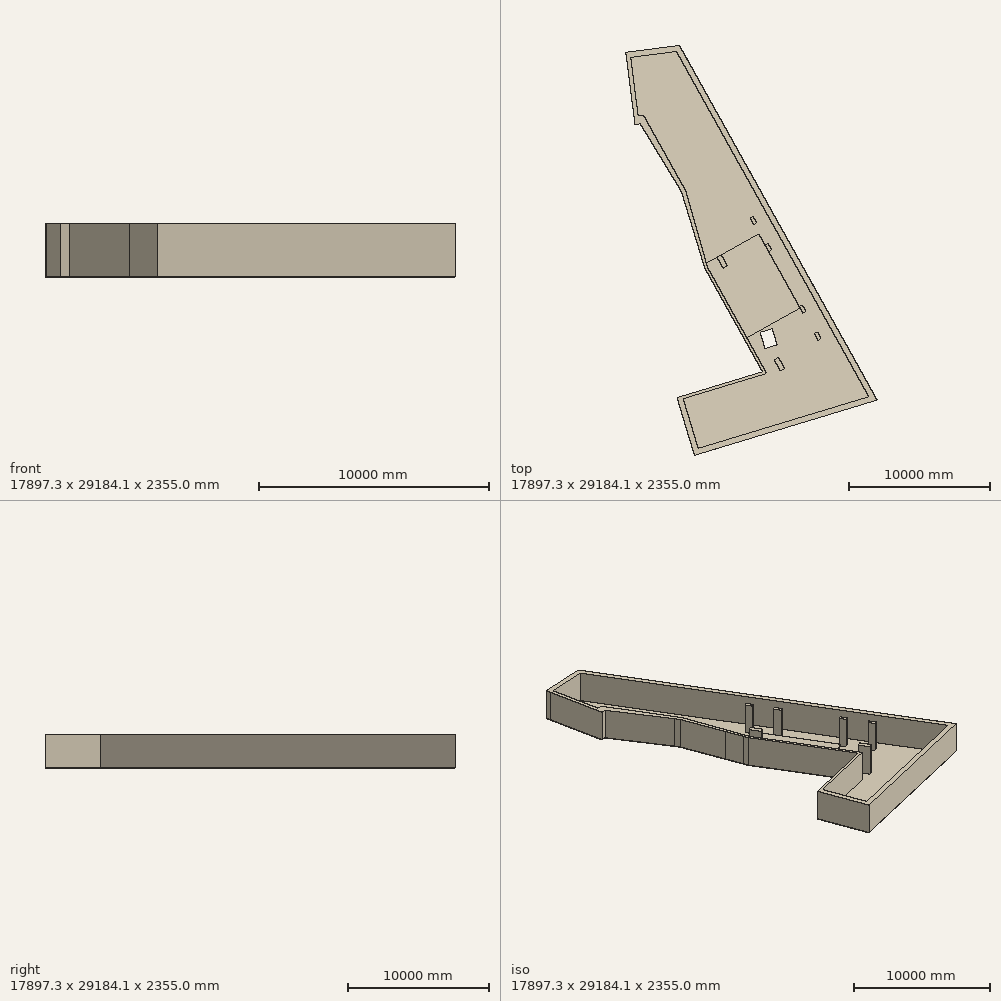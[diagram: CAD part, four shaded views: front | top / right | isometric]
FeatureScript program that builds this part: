
annotation { "Feature Type Name" : "Feature", "Feature Type Description" : "" }
export const myFeature = defineFeature(function(context is Context, id is Id, definition is map)
    precondition{}
    {
        {
            assignVariable(context, id + "F0", {"name" : "Ceiling", "anyValue" : 1890 + 440});
        }
        {
            var Q0;
            Q0=qCreatedBy(makeId("Top.planeOp"),FACE);
            var sketch = newSketch(context, id + "F1", { "sketchPlane" : qUnion([Q0])});
            skLineSegment(sketch, "E0", {"start": v(50356.24, 60225.68) * mm, "end": v(49220.2, 59881.82) * mm});
            skLineSegment(sketch, "E1", {"start": v(49220.2, 59881.82) * mm, "end": v(48658.24, 61738.46) * mm});
            skLineSegment(sketch, "E2", {"start": v(48658.24, 61738.46) * mm, "end": v(48436.53, 61671.35) * mm});
            skLineSegment(sketch, "E3", {"start": v(48436.53, 61671.35) * mm, "end": v(48364.1, 61910.63) * mm});
            skLineSegment(sketch, "E4", {"start": v(48364.1, 61910.63) * mm, "end": v(47885.55, 61765.78) * mm});
            skLineSegment(sketch, "E5", {"start": v(47885.55, 61765.78) * mm, "end": v(47957.97, 61526.5) * mm});
            skLineSegment(sketch, "E6", {"start": v(47957.97, 61526.5) * mm, "end": v(47686.86, 61444.44) * mm});
            skLineSegment(sketch, "E7", {"start": v(47686.86, 61444.44) * mm, "end": v(47759.29, 61205.16) * mm});
            skLineSegment(sketch, "E8", {"start": v(47759.29, 61205.16) * mm, "end": v(48491.38, 61426.75) * mm});
            skLineSegment(sketch, "E9", {"start": v(48491.38, 61426.75) * mm, "end": v(49070.78, 59512.52) * mm});
            skLineSegment(sketch, "E10", {"start": v(49070.78, 59512.52) * mm, "end": v(46721.47, 58801.43) * mm});
            skLineSegment(sketch, "E11", {"start": v(46721.47, 58801.43) * mm, "end": v(46142.07, 60715.66) * mm});
            skLineSegment(sketch, "E12", {"start": v(46142.07, 60715.66) * mm, "end": v(46706.46, 60886.5) * mm});
            skLineSegment(sketch, "E13", {"start": v(46706.46, 60886.5) * mm, "end": v(46634.03, 61125.77) * mm});
            skLineSegment(sketch, "E14", {"start": v(46634.03, 61125.77) * mm, "end": v(45451.68, 60767.9) * mm});
            skLineSegment(sketch, "E15", {"start": v(45451.68, 60767.9) * mm, "end": v(45524.1, 60528.62) * mm});
            skLineSegment(sketch, "E16", {"start": v(45524.1, 60528.62) * mm, "end": v(44643.85, 60262.18) * mm});
            skLineSegment(sketch, "E17", {"start": v(44643.85, 60262.18) * mm, "end": v(44571.42, 60501.46) * mm});
            skLineSegment(sketch, "E18", {"start": v(44571.42, 60501.46) * mm, "end": v(43824.87, 60275.5) * mm});
            skLineSegment(sketch, "E19", {"start": v(43824.87, 60275.5) * mm, "end": v(44386.83, 58418.88) * mm});
            skLineSegment(sketch, "E20", {"start": v(44386.83, 58418.88) * mm, "end": v(39132.43, 56828.48) * mm});
            skLineSegment(sketch, "E21", {"start": v(39132.43, 56828.48) * mm, "end": v(39132.43, 56828.48) * mm});
            skLineSegment(sketch, "E22", {"start": v(39132.43, 56828.48) * mm, "end": v(38458.91, 56624.62) * mm});
            skLineSegment(sketch, "E23", {"start": v(38458.91, 56624.62) * mm, "end": v(38574.8, 56241.77) * mm});
            skLineSegment(sketch, "E24", {"start": v(38574.8, 56241.77) * mm, "end": v(39350, 53680.63) * mm});
            skLineSegment(sketch, "E25", {"start": v(39350, 53680.63) * mm, "end": v(39348.17, 53681.01) * mm});
            skLineSegment(sketch, "E26", {"start": v(39348.17, 53681.01) * mm, "end": v(39517.02, 53123.18) * mm});
            skLineSegment(sketch, "E27", {"start": v(39517.02, 53123.18) * mm, "end": v(36984.61, 52356.67) * mm});
            skLineSegment(sketch, "E28", {"start": v(36984.61, 52356.67) * mm, "end": v(36288.15, 54657.64) * mm});
            skLineSegment(sketch, "E29", {"start": v(36288.15, 54657.64) * mm, "end": v(36288.98, 54657.9) * mm});
            skLineSegment(sketch, "E30", {"start": v(36288.98, 54657.9) * mm, "end": v(35925.26, 55857.73) * mm});
            skLineSegment(sketch, "E31", {"start": v(35925.26, 55857.73) * mm, "end": v(30957.21, 72270.12) * mm});
            skLineSegment(sketch, "E32", {"start": v(30957.21, 72270.12) * mm, "end": v(52856.55, 75078.33) * mm});
            skLineSegment(sketch, "E33", {"start": v(52856.55, 75078.33) * mm, "end": v(64538.41, 54127.57) * mm});
            skLineSegment(sketch, "E34", {"start": v(64538.41, 54127.57) * mm, "end": v(66559.72, 50502.1) * mm});
            skLineSegment(sketch, "E35", {"start": v(66559.72, 50502.1) * mm, "end": v(54412.26, 46825.31) * mm});
            skLineSegment(sketch, "E36", {"start": v(54412.26, 46825.31) * mm, "end": v(53342.81, 50358.57) * mm});
            skLineSegment(sketch, "E37", {"start": v(53342.81, 50358.57) * mm, "end": v(59288.18, 52158.11) * mm});
            skLineSegment(sketch, "E38", {"start": v(59288.18, 52158.11) * mm, "end": v(59106.76, 52483.52) * mm});
            skLineSegment(sketch, "E39", {"start": v(59106.76, 52483.52) * mm, "end": v(55867.2, 58292.84) * mm});
            skLineSegment(sketch, "E40", {"start": v(55867.2, 58292.84) * mm, "end": v(51354.69, 56926.99) * mm});
            skLineSegment(sketch, "E41", {"start": v(51354.69, 56926.99) * mm, "end": v(50356.24, 60225.68) * mm});
            skCircle(sketch, "E42", {"center": v(0, 0) * mm, "radius": 1927.6 * mm});
            skLineSegment(sketch, "E43", {"start": v(0, 5000) * mm, "end": v(0, -5000) * mm});
            skLineSegment(sketch, "E44", {"start": v(5000, 0) * mm, "end": v(-5000, 0) * mm});
            skLineSegment(sketch, "E45", {"start": v(52857.63, 75079.51) * mm, "end": v(52856.55, 75078.33) * mm});
            skLineSegment(sketch, "E46", {"start": v(52856.55, 75078.33) * mm, "end": v(56743.09, 68109.43) * mm});
            skLineSegment(sketch, "E47", {"start": v(56743.09, 68109.43) * mm, "end": v(52142.28, 67923.68) * mm});
            skLineSegment(sketch, "E48", {"start": v(52142.28, 67923.68) * mm, "end": v(32512.63, 67131.17) * mm});
            skLineSegment(sketch, "E49", {"start": v(32512.63, 67131.17) * mm, "end": v(32512.63, 67131.18) * mm});
            skLineSegment(sketch, "E50", {"start": v(32512.63, 67131.18) * mm, "end": v(30957.18, 72270.11) * mm});
            skLineSegment(sketch, "E51", {"start": v(30957.18, 72270.11) * mm, "end": v(49304.34, 74623.7) * mm});
            skLineSegment(sketch, "E52", {"start": v(49304.34, 74623.7) * mm, "end": v(49304.34, 74623.69) * mm});
            skLineSegment(sketch, "E53", {"start": v(49304.34, 74623.69) * mm, "end": v(51228.96, 74870.57) * mm});
            skLineSegment(sketch, "E54", {"start": v(51228.96, 74870.57) * mm, "end": v(52856, 75079.3) * mm});
            skLineSegment(sketch, "E55", {"start": v(44184.43, 60123.13) * mm, "end": v(45964.6, 60661.95) * mm});
            skLineSegment(sketch, "E56", {"start": v(45964.6, 60661.95) * mm, "end": v(46549.88, 58728.5) * mm});
            skLineSegment(sketch, "E57", {"start": v(46549.88, 58728.5) * mm, "end": v(44769.56, 58189.64) * mm});
            skLineSegment(sketch, "E58", {"start": v(44769.56, 58189.64) * mm, "end": v(44184.43, 60123.12) * mm});
            skLineSegment(sketch, "E59", {"start": v(44184.43, 60123.12) * mm, "end": v(44184.43, 60123.13) * mm});
            skLineSegment(sketch, "E60", {"start": v(35925.26, 55857.73) * mm, "end": v(32512.63, 67131.18) * mm});
            skLineSegment(sketch, "E61", {"start": v(32512.63, 67131.18) * mm, "end": v(56743.09, 68109.43) * mm});
            skLineSegment(sketch, "E62", {"start": v(56743.09, 68109.43) * mm, "end": v(64538.41, 54127.57) * mm});
            skLineSegment(sketch, "E63", {"start": v(53342.81, 50358.57) * mm, "end": v(51750.13, 55620.52) * mm});
            skLineSegment(sketch, "E64", {"start": v(51750.13, 55620.52) * mm, "end": v(52375.23, 55809.73) * mm});
            skLineSegment(sketch, "E65", {"start": v(52375.23, 55809.73) * mm, "end": v(53909.98, 50739.2) * mm});
            skLineSegment(sketch, "E66", {"start": v(53909.98, 50739.2) * mm, "end": v(57604, 51858.9) * mm});
            skLineSegment(sketch, "E67", {"start": v(57604, 51858.9) * mm, "end": v(55674.23, 58234.43) * mm});
            skLineSegment(sketch, "E68", {"start": v(55674.23, 58234.43) * mm, "end": v(51354.69, 56926.99) * mm});
            skLineSegment(sketch, "E69", {"start": v(51354.69, 56926.99) * mm, "end": v(55674.23, 58234.43) * mm});
            skLineSegment(sketch, "E70", {"start": v(55674.23, 58234.43) * mm, "end": v(57604.42, 51857.43) * mm});
            skLineSegment(sketch, "E71", {"start": v(57604.42, 51857.43) * mm, "end": v(53909.98, 50739.2) * mm});
            skLineSegment(sketch, "E72", {"start": v(53909.98, 50739.2) * mm, "end": v(52375.23, 55809.73) * mm});
            skLineSegment(sketch, "E73", {"start": v(52375.23, 55809.73) * mm, "end": v(51750.13, 55620.52) * mm});
            skLineSegment(sketch, "E74", {"start": v(51750.13, 55620.52) * mm, "end": v(51354.69, 56926.99) * mm});
            skLineSegment(sketch, "E75", {"start": v(43785.9, 47980.97) * mm, "end": v(41725.14, 54896.4) * mm});
            skLineSegment(sketch, "E76", {"start": v(41725.14, 54896.4) * mm, "end": v(48582.16, 57001.67) * mm});
            skLineSegment(sketch, "E77", {"start": v(48582.16, 57001.67) * mm, "end": v(50679.83, 50071.15) * mm});
            skLineSegment(sketch, "E78", {"start": v(50679.83, 50071.15) * mm, "end": v(47628.14, 49145.9) * mm});
            skLineSegment(sketch, "E79", {"start": v(47628.14, 49145.9) * mm, "end": v(47641.24, 49102.68) * mm});
            skLineSegment(sketch, "E80", {"start": v(47641.24, 49102.68) * mm, "end": v(46838.37, 48859.26) * mm});
            skLineSegment(sketch, "E81", {"start": v(46838.37, 48859.26) * mm, "end": v(46825.27, 48902.48) * mm});
            skLineSegment(sketch, "E82", {"start": v(46825.27, 48902.48) * mm, "end": v(43785.9, 47980.97) * mm});
            skLineSegment(sketch, "E83", {"start": v(43985.95, 48355.1) * mm, "end": v(50305.83, 50271.24) * mm});
            skLineSegment(sketch, "E84", {"start": v(43784.47, 47980.54) * mm, "end": v(50679.83, 50071.15) * mm});
            skLineSegment(sketch, "E85", {"start": v(42097.56, 54696.9) * mm, "end": v(43985.95, 48355.1) * mm});
            skLineSegment(sketch, "E86", {"start": v(41725.14, 54896.4) * mm, "end": v(43784.47, 47980.54) * mm});
            skLineSegment(sketch, "E87", {"start": v(48382.3, 56626.46) * mm, "end": v(42097.56, 54696.9) * mm});
            skLineSegment(sketch, "E88", {"start": v(48582.17, 57001.65) * mm, "end": v(41725.14, 54896.4) * mm});
            skLineSegment(sketch, "E89", {"start": v(50305.83, 50271.24) * mm, "end": v(48382.3, 56626.46) * mm});
            skLineSegment(sketch, "E90", {"start": v(50679.83, 50071.15) * mm, "end": v(48582.17, 57001.65) * mm});
            skLineSegment(sketch, "E91", {"start": v(57792.28, 52268.48) * mm, "end": v(58968.18, 52624.48) * mm});
            skLineSegment(sketch, "E92", {"start": v(59098.58, 52193.79) * mm, "end": v(58968.18, 52624.48) * mm});
            skLineSegment(sketch, "E93", {"start": v(57922.67, 51837.79) * mm, "end": v(59098.58, 52193.79) * mm});
            skLineSegment(sketch, "E94", {"start": v(57922.67, 51837.79) * mm, "end": v(57792.28, 52268.48) * mm});
            skLineSegment(sketch, "E95", {"start": v(61899.36, 49097.97) * mm, "end": v(50281.68, 69933.64) * mm});
            skLineSegment(sketch, "E96", {"start": v(55070.83, 59721.1) * mm, "end": v(59287.5, 52158.7) * mm});
            skLineSegment(sketch, "E97", {"start": v(54896.15, 59623.7) * mm, "end": v(58991.9, 52278.2) * mm});
            skLineSegment(sketch, "E98", {"start": v(55911.81, 59846.47) * mm, "end": v(50927.73, 58337.56) * mm});
            skLineSegment(sketch, "E99", {"start": v(51575.28, 74914.98) * mm, "end": v(49601.81, 74661.66) * mm});
            skLineSegment(sketch, "E100", {"start": v(49601.81, 74661.66) * mm, "end": v(50012.55, 71444.1) * mm});
            skLineSegment(sketch, "E101", {"start": v(50012.55, 71444.1) * mm, "end": v(62198.73, 49586.37) * mm});
            skLineSegment(sketch, "E102", {"start": v(62198.73, 49586.37) * mm, "end": v(64867.16, 51074.04) * mm});
            skLineSegment(sketch, "E103", {"start": v(64867.16, 51074.04) * mm, "end": v(51575.28, 74914.98) * mm});
            skLineSegment(sketch, "E104", {"start": v(51980.16, 57115.1) * mm, "end": v(55674.65, 58233.32) * mm});
            skLineSegment(sketch, "E105", {"start": v(55674.65, 58233.32) * mm, "end": v(57604, 51858.9) * mm});
            skLineSegment(sketch, "E106", {"start": v(57604, 51858.9) * mm, "end": v(53909.52, 50740.69) * mm});
            skLineSegment(sketch, "E107", {"start": v(53909.52, 50740.69) * mm, "end": v(51980.16, 57115.1) * mm});
            skLineSegment(sketch, "E108", {"start": v(55694.63, 56724.4) * mm, "end": v(55675.8, 56786.62) * mm});
            skLineSegment(sketch, "E109", {"start": v(55675.8, 56786.62) * mm, "end": v(55672.2, 56785.53) * mm});
            skArc(sketch, "E110", {"start": v(55672.2, 56785.53) * mm, "mid": v(55669.63, 56783.5) * mm, "end": v(55669.12, 56780.27) * mm});
            skLineSegment(sketch, "E111", {"start": v(55669.12, 56780.27) * mm, "end": v(55678.43, 56737.44) * mm});
            skArc(sketch, "E112", {"start": v(55671.21, 56725.15) * mm, "mid": v(55677.22, 56729.88) * mm, "end": v(55678.43, 56737.44) * mm});
            skLineSegment(sketch, "E113", {"start": v(55671.21, 56725.15) * mm, "end": v(55560.55, 56691.66) * mm});
            skArc(sketch, "E114", {"start": v(55547.74, 56697.88) * mm, "mid": v(55552.93, 56692.26) * mm, "end": v(55560.55, 56691.66) * mm});
            skLineSegment(sketch, "E115", {"start": v(55547.74, 56697.88) * mm, "end": v(55531.74, 56738.69) * mm});
            skArc(sketch, "E116", {"start": v(55531.74, 56738.69) * mm, "mid": v(55529.51, 56741.1) * mm, "end": v(55526.24, 56741.35) * mm});
            skLineSegment(sketch, "E117", {"start": v(55526.24, 56741.35) * mm, "end": v(55522.66, 56740.27) * mm});
            skLineSegment(sketch, "E118", {"start": v(55522.66, 56740.27) * mm, "end": v(55541.49, 56678.05) * mm});
            skLineSegment(sketch, "E119", {"start": v(55541.49, 56678.05) * mm, "end": v(55694.63, 56724.4) * mm});
            skLineSegment(sketch, "E120", {"start": v(55616.8, 56429.2) * mm, "end": v(55635.64, 56366.99) * mm});
            skLineSegment(sketch, "E121", {"start": v(55635.64, 56366.99) * mm, "end": v(55639.22, 56368.08) * mm});
            skArc(sketch, "E122", {"start": v(55639.22, 56368.08) * mm, "mid": v(55641.8, 56370.1) * mm, "end": v(55642.32, 56373.34) * mm});
            skLineSegment(sketch, "E123", {"start": v(55642.32, 56373.34) * mm, "end": v(55633, 56416.17) * mm});
            skArc(sketch, "E124", {"start": v(55640.22, 56428.45) * mm, "mid": v(55634.2, 56423.72) * mm, "end": v(55633, 56416.17) * mm});
            skLineSegment(sketch, "E125", {"start": v(55640.22, 56428.45) * mm, "end": v(55750.88, 56461.95) * mm});
            skArc(sketch, "E126", {"start": v(55763.7, 56455.73) * mm, "mid": v(55758.5, 56461.34) * mm, "end": v(55750.88, 56461.95) * mm});
            skLineSegment(sketch, "E127", {"start": v(55763.7, 56455.73) * mm, "end": v(55779.7, 56414.92) * mm});
            skArc(sketch, "E128", {"start": v(55779.7, 56414.92) * mm, "mid": v(55781.92, 56412.51) * mm, "end": v(55785.19, 56412.26) * mm});
            skLineSegment(sketch, "E129", {"start": v(55785.19, 56412.26) * mm, "end": v(55788.78, 56413.34) * mm});
            skLineSegment(sketch, "E130", {"start": v(55788.78, 56413.34) * mm, "end": v(55769.95, 56475.55) * mm});
            skLineSegment(sketch, "E131", {"start": v(55769.95, 56475.55) * mm, "end": v(55616.8, 56429.2) * mm});
            skCircle(sketch, "E132", {"center": v(55655.72, 56576.8) * mm, "radius": 0.25 * mm});
            skCircle(sketch, "E133", {"center": v(55733.93, 56318.38) * mm, "radius": 9 * mm});
            skCircle(sketch, "E134", {"center": v(55577.5, 56835.23) * mm, "radius": 9 * mm});
            skCircle(sketch, "E135", {"center": v(55405.22, 56783.08) * mm, "radius": 9 * mm});
            skCircle(sketch, "E136", {"center": v(55561.65, 56266.24) * mm, "radius": 9 * mm});
            skLineSegment(sketch, "E137", {"start": v(55367.81, 56803.1) * mm, "end": v(55654.95, 56890.01) * mm});
            skLineSegment(sketch, "E138", {"start": v(55541.63, 56228.83) * mm, "end": v(55367.81, 56803.1) * mm});
            skLineSegment(sketch, "E139", {"start": v(55828.76, 56315.74) * mm, "end": v(55541.63, 56228.83) * mm});
            skLineSegment(sketch, "E140", {"start": v(55654.95, 56890.01) * mm, "end": v(55828.76, 56315.74) * mm});
            skCircle(sketch, "E141", {"center": v(55655.72, 56576.8) * mm, "radius": 57.5 * mm});
            skCircle(sketch, "E142", {"center": v(55655.72, 56576.8) * mm, "radius": 59.5 * mm});
            skCircle(sketch, "E143", {"center": v(55655.72, 56576.8) * mm, "radius": 63.5 * mm});
            skLineSegment(sketch, "E144", {"start": v(55607.5, 56356.38) * mm, "end": v(55636.22, 56365.08) * mm});
            skLineSegment(sketch, "E145", {"start": v(55636.22, 56365.08) * mm, "end": v(55621.73, 56412.93) * mm});
            skLineSegment(sketch, "E146", {"start": v(55621.73, 56412.93) * mm, "end": v(55593.02, 56404.24) * mm});
            skLineSegment(sketch, "E147", {"start": v(55593.02, 56404.24) * mm, "end": v(55607.5, 56356.38) * mm});
            skLineSegment(sketch, "E148", {"start": v(55636.22, 56365.08) * mm, "end": v(55635.64, 56366.99) * mm});
            skLineSegment(sketch, "E149", {"start": v(55635.64, 56366.99) * mm, "end": v(55621.73, 56412.93) * mm});
            skLineSegment(sketch, "E150", {"start": v(52875.62, 55599.52) * mm, "end": v(52894.45, 55537.3) * mm});
            skLineSegment(sketch, "E151", {"start": v(52894.45, 55537.3) * mm, "end": v(52898.03, 55538.4) * mm});
            skArc(sketch, "E152", {"start": v(52898.03, 55538.4) * mm, "mid": v(52900.6, 55540.42) * mm, "end": v(52901.13, 55543.66) * mm});
            skLineSegment(sketch, "E153", {"start": v(52901.13, 55543.66) * mm, "end": v(52891.81, 55586.5) * mm});
            skArc(sketch, "E154", {"start": v(52899.03, 55598.77) * mm, "mid": v(52893.02, 55594.04) * mm, "end": v(52891.81, 55586.5) * mm});
            skLineSegment(sketch, "E155", {"start": v(52899.03, 55598.77) * mm, "end": v(53009.69, 55632.26) * mm});
            skArc(sketch, "E156", {"start": v(53022.5, 55626.05) * mm, "mid": v(53017.31, 55631.66) * mm, "end": v(53009.69, 55632.26) * mm});
            skLineSegment(sketch, "E157", {"start": v(53022.5, 55626.05) * mm, "end": v(53038.5, 55585.24) * mm});
            skArc(sketch, "E158", {"start": v(53038.5, 55585.24) * mm, "mid": v(53040.73, 55582.83) * mm, "end": v(53044, 55582.57) * mm});
            skLineSegment(sketch, "E159", {"start": v(53044, 55582.57) * mm, "end": v(53047.59, 55583.66) * mm});
            skLineSegment(sketch, "E160", {"start": v(53047.59, 55583.66) * mm, "end": v(53028.76, 55645.87) * mm});
            skLineSegment(sketch, "E161", {"start": v(53028.76, 55645.87) * mm, "end": v(52875.62, 55599.52) * mm});
            skLineSegment(sketch, "E162", {"start": v(52953.44, 55894.72) * mm, "end": v(52934.6, 55956.94) * mm});
            skLineSegment(sketch, "E163", {"start": v(52934.6, 55956.94) * mm, "end": v(52931.02, 55955.85) * mm});
            skArc(sketch, "E164", {"start": v(52931.02, 55955.85) * mm, "mid": v(52928.44, 55953.82) * mm, "end": v(52927.92, 55950.59) * mm});
            skLineSegment(sketch, "E165", {"start": v(52927.92, 55950.59) * mm, "end": v(52937.24, 55907.75) * mm});
            skArc(sketch, "E166", {"start": v(52930.02, 55895.47) * mm, "mid": v(52936.03, 55900.2) * mm, "end": v(52937.24, 55907.75) * mm});
            skLineSegment(sketch, "E167", {"start": v(52930.02, 55895.47) * mm, "end": v(52819.36, 55861.98) * mm});
            skArc(sketch, "E168", {"start": v(52806.55, 55868.2) * mm, "mid": v(52811.74, 55862.58) * mm, "end": v(52819.36, 55861.98) * mm});
            skLineSegment(sketch, "E169", {"start": v(52806.55, 55868.2) * mm, "end": v(52790.55, 55909) * mm});
            skArc(sketch, "E170", {"start": v(52790.55, 55909) * mm, "mid": v(52788.32, 55911.41) * mm, "end": v(52785.05, 55911.67) * mm});
            skLineSegment(sketch, "E171", {"start": v(52785.05, 55911.67) * mm, "end": v(52781.47, 55910.59) * mm});
            skLineSegment(sketch, "E172", {"start": v(52781.47, 55910.59) * mm, "end": v(52800.3, 55848.37) * mm});
            skLineSegment(sketch, "E173", {"start": v(52800.3, 55848.37) * mm, "end": v(52953.44, 55894.72) * mm});
            skCircle(sketch, "E174", {"center": v(52914.53, 55747.12) * mm, "radius": 0.25 * mm});
            skCircle(sketch, "E175", {"center": v(52836.3, 56005.54) * mm, "radius": 9 * mm});
            skCircle(sketch, "E176", {"center": v(52992.74, 55488.7) * mm, "radius": 9 * mm});
            skCircle(sketch, "E177", {"center": v(53165.02, 55540.84) * mm, "radius": 9 * mm});
            skCircle(sketch, "E178", {"center": v(53008.6, 56057.69) * mm, "radius": 9 * mm});
            skLineSegment(sketch, "E179", {"start": v(53202.43, 55520.82) * mm, "end": v(52915.3, 55433.91) * mm});
            skLineSegment(sketch, "E180", {"start": v(53028.61, 56095.1) * mm, "end": v(53202.43, 55520.82) * mm});
            skLineSegment(sketch, "E181", {"start": v(52741.48, 56008.19) * mm, "end": v(53028.61, 56095.1) * mm});
            skLineSegment(sketch, "E182", {"start": v(52915.3, 55433.91) * mm, "end": v(52741.48, 56008.19) * mm});
            skCircle(sketch, "E183", {"center": v(52914.53, 55747.12) * mm, "radius": 57.5 * mm});
            skCircle(sketch, "E184", {"center": v(52914.53, 55747.12) * mm, "radius": 59.5 * mm});
            skCircle(sketch, "E185", {"center": v(52914.53, 55747.12) * mm, "radius": 63.5 * mm});
            skLineSegment(sketch, "E186", {"start": v(53045.04, 55592.08) * mm, "end": v(53073.75, 55600.77) * mm});
            skLineSegment(sketch, "E187", {"start": v(53073.75, 55600.77) * mm, "end": v(53062.4, 55638.3) * mm});
            skLineSegment(sketch, "E188", {"start": v(53062.4, 55638.3) * mm, "end": v(53033.68, 55629.6) * mm});
            skLineSegment(sketch, "E189", {"start": v(53033.68, 55629.6) * mm, "end": v(53045.04, 55592.08) * mm});
            skLineSegment(sketch, "E190", {"start": v(53076.88, 55590.44) * mm, "end": v(53073.75, 55600.77) * mm});
            skLineSegment(sketch, "E191", {"start": v(53048.16, 55581.75) * mm, "end": v(53076.88, 55590.44) * mm});
            skLineSegment(sketch, "E192", {"start": v(53048.16, 55581.75) * mm, "end": v(53047.59, 55583.66) * mm});
            skLineSegment(sketch, "E193", {"start": v(53602.75, 53197.13) * mm, "end": v(53621.58, 53134.91) * mm});
            skLineSegment(sketch, "E194", {"start": v(53621.58, 53134.91) * mm, "end": v(53625.16, 53136) * mm});
            skArc(sketch, "E195", {"start": v(53625.16, 53136) * mm, "mid": v(53627.74, 53138.03) * mm, "end": v(53628.26, 53141.26) * mm});
            skLineSegment(sketch, "E196", {"start": v(53628.26, 53141.26) * mm, "end": v(53618.94, 53184.1) * mm});
            skArc(sketch, "E197", {"start": v(53626.16, 53196.38) * mm, "mid": v(53620.15, 53191.65) * mm, "end": v(53618.94, 53184.1) * mm});
            skLineSegment(sketch, "E198", {"start": v(53626.16, 53196.38) * mm, "end": v(53736.82, 53229.87) * mm});
            skArc(sketch, "E199", {"start": v(53749.63, 53223.65) * mm, "mid": v(53744.44, 53229.27) * mm, "end": v(53736.82, 53229.87) * mm});
            skLineSegment(sketch, "E200", {"start": v(53749.63, 53223.65) * mm, "end": v(53765.64, 53182.84) * mm});
            skArc(sketch, "E201", {"start": v(53765.64, 53182.84) * mm, "mid": v(53767.86, 53180.44) * mm, "end": v(53771.13, 53180.18) * mm});
            skLineSegment(sketch, "E202", {"start": v(53771.13, 53180.18) * mm, "end": v(53774.72, 53181.26) * mm});
            skLineSegment(sketch, "E203", {"start": v(53774.72, 53181.26) * mm, "end": v(53755.89, 53243.48) * mm});
            skLineSegment(sketch, "E204", {"start": v(53755.89, 53243.48) * mm, "end": v(53602.75, 53197.13) * mm});
            skLineSegment(sketch, "E205", {"start": v(53680.56, 53492.33) * mm, "end": v(53661.73, 53554.54) * mm});
            skLineSegment(sketch, "E206", {"start": v(53661.73, 53554.54) * mm, "end": v(53658.15, 53553.46) * mm});
            skArc(sketch, "E207", {"start": v(53658.15, 53553.46) * mm, "mid": v(53655.57, 53551.43) * mm, "end": v(53655.05, 53548.2) * mm});
            skLineSegment(sketch, "E208", {"start": v(53655.05, 53548.2) * mm, "end": v(53664.37, 53505.36) * mm});
            skArc(sketch, "E209", {"start": v(53657.15, 53493.08) * mm, "mid": v(53663.16, 53497.8) * mm, "end": v(53664.37, 53505.36) * mm});
            skLineSegment(sketch, "E210", {"start": v(53657.15, 53493.08) * mm, "end": v(53546.5, 53459.59) * mm});
            skArc(sketch, "E211", {"start": v(53533.68, 53465.8) * mm, "mid": v(53538.87, 53460.19) * mm, "end": v(53546.5, 53459.59) * mm});
            skLineSegment(sketch, "E212", {"start": v(53533.68, 53465.8) * mm, "end": v(53517.68, 53506.61) * mm});
            skArc(sketch, "E213", {"start": v(53517.68, 53506.61) * mm, "mid": v(53515.45, 53509.02) * mm, "end": v(53512.18, 53509.28) * mm});
            skLineSegment(sketch, "E214", {"start": v(53512.18, 53509.28) * mm, "end": v(53508.6, 53508.2) * mm});
            skLineSegment(sketch, "E215", {"start": v(53508.6, 53508.2) * mm, "end": v(53527.43, 53445.98) * mm});
            skLineSegment(sketch, "E216", {"start": v(53527.43, 53445.98) * mm, "end": v(53680.56, 53492.33) * mm});
            skCircle(sketch, "E217", {"center": v(53641.66, 53344.73) * mm, "radius": 0.25 * mm});
            skCircle(sketch, "E218", {"center": v(53563.44, 53603.15) * mm, "radius": 9 * mm});
            skCircle(sketch, "E219", {"center": v(53719.87, 53086.3) * mm, "radius": 9 * mm});
            skCircle(sketch, "E220", {"center": v(53892.15, 53138.45) * mm, "radius": 9 * mm});
            skCircle(sketch, "E221", {"center": v(53735.72, 53655.3) * mm, "radius": 9 * mm});
            skLineSegment(sketch, "E222", {"start": v(53929.56, 53118.43) * mm, "end": v(53642.42, 53031.52) * mm});
            skLineSegment(sketch, "E223", {"start": v(53755.74, 53692.7) * mm, "end": v(53929.56, 53118.43) * mm});
            skLineSegment(sketch, "E224", {"start": v(53468.6, 53605.8) * mm, "end": v(53755.74, 53692.7) * mm});
            skLineSegment(sketch, "E225", {"start": v(53642.42, 53031.52) * mm, "end": v(53468.6, 53605.8) * mm});
            skCircle(sketch, "E226", {"center": v(53641.66, 53344.73) * mm, "radius": 57.5 * mm});
            skCircle(sketch, "E227", {"center": v(53641.66, 53344.73) * mm, "radius": 59.5 * mm});
            skCircle(sketch, "E228", {"center": v(53641.66, 53344.73) * mm, "radius": 63.5 * mm});
            skLineSegment(sketch, "E229", {"start": v(53689.87, 53565.15) * mm, "end": v(53661.16, 53556.46) * mm});
            skLineSegment(sketch, "E230", {"start": v(53661.16, 53556.46) * mm, "end": v(53675.64, 53508.6) * mm});
            skLineSegment(sketch, "E231", {"start": v(53675.64, 53508.6) * mm, "end": v(53704.35, 53517.3) * mm});
            skLineSegment(sketch, "E232", {"start": v(53704.35, 53517.3) * mm, "end": v(53689.87, 53565.15) * mm});
            skLineSegment(sketch, "E233", {"start": v(53661.16, 53556.46) * mm, "end": v(53661.73, 53554.54) * mm});
            skLineSegment(sketch, "E234", {"start": v(53661.73, 53554.54) * mm, "end": v(53675.64, 53508.6) * mm});
            skLineSegment(sketch, "E235", {"start": v(56421.76, 54322) * mm, "end": v(56402.93, 54384.22) * mm});
            skLineSegment(sketch, "E236", {"start": v(56402.93, 54384.22) * mm, "end": v(56399.34, 54383.14) * mm});
            skArc(sketch, "E237", {"start": v(56399.34, 54383.14) * mm, "mid": v(56396.76, 54381.1) * mm, "end": v(56396.24, 54377.87) * mm});
            skLineSegment(sketch, "E238", {"start": v(56396.24, 54377.87) * mm, "end": v(56405.56, 54335.04) * mm});
            skArc(sketch, "E239", {"start": v(56398.34, 54322.76) * mm, "mid": v(56404.35, 54327.49) * mm, "end": v(56405.56, 54335.04) * mm});
            skLineSegment(sketch, "E240", {"start": v(56398.34, 54322.76) * mm, "end": v(56287.68, 54289.27) * mm});
            skArc(sketch, "E241", {"start": v(56274.87, 54295.48) * mm, "mid": v(56280.06, 54289.87) * mm, "end": v(56287.68, 54289.27) * mm});
            skLineSegment(sketch, "E242", {"start": v(56274.87, 54295.48) * mm, "end": v(56258.87, 54336.3) * mm});
            skArc(sketch, "E243", {"start": v(56258.87, 54336.3) * mm, "mid": v(56256.64, 54338.7) * mm, "end": v(56253.37, 54338.96) * mm});
            skLineSegment(sketch, "E244", {"start": v(56253.37, 54338.96) * mm, "end": v(56249.79, 54337.87) * mm});
            skLineSegment(sketch, "E245", {"start": v(56249.79, 54337.87) * mm, "end": v(56268.62, 54275.66) * mm});
            skLineSegment(sketch, "E246", {"start": v(56268.62, 54275.66) * mm, "end": v(56421.76, 54322) * mm});
            skLineSegment(sketch, "E247", {"start": v(56343.94, 54026.8) * mm, "end": v(56362.77, 53964.6) * mm});
            skLineSegment(sketch, "E248", {"start": v(56362.77, 53964.6) * mm, "end": v(56366.35, 53965.68) * mm});
            skArc(sketch, "E249", {"start": v(56366.35, 53965.68) * mm, "mid": v(56368.93, 53967.7) * mm, "end": v(56369.45, 53970.94) * mm});
            skLineSegment(sketch, "E250", {"start": v(56369.45, 53970.94) * mm, "end": v(56360.13, 54013.78) * mm});
            skArc(sketch, "E251", {"start": v(56367.35, 54026.06) * mm, "mid": v(56361.34, 54021.33) * mm, "end": v(56360.13, 54013.78) * mm});
            skLineSegment(sketch, "E252", {"start": v(56367.35, 54026.06) * mm, "end": v(56478, 54059.55) * mm});
            skArc(sketch, "E253", {"start": v(56490.82, 54053.33) * mm, "mid": v(56485.63, 54058.95) * mm, "end": v(56478, 54059.55) * mm});
            skLineSegment(sketch, "E254", {"start": v(56490.82, 54053.33) * mm, "end": v(56506.83, 54012.52) * mm});
            skArc(sketch, "E255", {"start": v(56506.83, 54012.52) * mm, "mid": v(56509.05, 54010.12) * mm, "end": v(56512.32, 54009.86) * mm});
            skLineSegment(sketch, "E256", {"start": v(56512.32, 54009.86) * mm, "end": v(56515.9, 54010.95) * mm});
            skLineSegment(sketch, "E257", {"start": v(56515.9, 54010.95) * mm, "end": v(56497.08, 54073.16) * mm});
            skLineSegment(sketch, "E258", {"start": v(56497.08, 54073.16) * mm, "end": v(56343.94, 54026.8) * mm});
            skCircle(sketch, "E259", {"center": v(56382.85, 54174.4) * mm, "radius": 0.25 * mm});
            skCircle(sketch, "E260", {"center": v(56461.06, 53915.99) * mm, "radius": 9 * mm});
            skCircle(sketch, "E261", {"center": v(56304.63, 54432.83) * mm, "radius": 9 * mm});
            skCircle(sketch, "E262", {"center": v(56132.35, 54380.69) * mm, "radius": 9 * mm});
            skCircle(sketch, "E263", {"center": v(56288.78, 53863.84) * mm, "radius": 9 * mm});
            skLineSegment(sketch, "E264", {"start": v(56094.94, 54400.7) * mm, "end": v(56382.08, 54487.62) * mm});
            skLineSegment(sketch, "E265", {"start": v(56268.76, 53826.44) * mm, "end": v(56094.94, 54400.7) * mm});
            skLineSegment(sketch, "E266", {"start": v(56555.9, 53913.35) * mm, "end": v(56268.76, 53826.44) * mm});
            skLineSegment(sketch, "E267", {"start": v(56382.08, 54487.62) * mm, "end": v(56555.9, 53913.35) * mm});
            skCircle(sketch, "E268", {"center": v(56382.85, 54174.4) * mm, "radius": 57.5 * mm});
            skCircle(sketch, "E269", {"center": v(56382.85, 54174.4) * mm, "radius": 59.5 * mm});
            skCircle(sketch, "E270", {"center": v(56382.85, 54174.4) * mm, "radius": 63.5 * mm});
            skLineSegment(sketch, "E271", {"start": v(56252.34, 54329.45) * mm, "end": v(56223.62, 54320.76) * mm});
            skLineSegment(sketch, "E272", {"start": v(56223.62, 54320.76) * mm, "end": v(56234.98, 54283.24) * mm});
            skLineSegment(sketch, "E273", {"start": v(56234.98, 54283.24) * mm, "end": v(56263.7, 54291.93) * mm});
            skLineSegment(sketch, "E274", {"start": v(56263.7, 54291.93) * mm, "end": v(56252.34, 54329.45) * mm});
            skLineSegment(sketch, "E275", {"start": v(56220.5, 54331.1) * mm, "end": v(56223.62, 54320.76) * mm});
            skLineSegment(sketch, "E276", {"start": v(56249.2, 54339.79) * mm, "end": v(56220.5, 54331.1) * mm});
            skLineSegment(sketch, "E277", {"start": v(56249.2, 54339.79) * mm, "end": v(56249.79, 54337.87) * mm});
            skLineSegment(sketch, "E278", {"start": v(57251.35, 51929.78) * mm, "end": v(57238.9, 51926.01) * mm});
            skLineSegment(sketch, "E279", {"start": v(57238.9, 51926.01) * mm, "end": v(57192.55, 52079.15) * mm});
            skLineSegment(sketch, "E280", {"start": v(57192.55, 52079.15) * mm, "end": v(57205, 52082.92) * mm});
            skLineSegment(sketch, "E281", {"start": v(57205, 52082.92) * mm, "end": v(57222.67, 52024.54) * mm});
            skArc(sketch, "E282", {"start": v(57222.67, 52024.54) * mm, "mid": v(57229.95, 52015.66) * mm, "end": v(57241.37, 52014.52) * mm});
            skLineSegment(sketch, "E283", {"start": v(57241.37, 52014.52) * mm, "end": v(57340.91, 52044.65) * mm});
            skArc(sketch, "E284", {"start": v(57340.91, 52044.65) * mm, "mid": v(57349.8, 52051.93) * mm, "end": v(57350.92, 52063.35) * mm});
            skLineSegment(sketch, "E285", {"start": v(57350.92, 52063.35) * mm, "end": v(57333.25, 52121.74) * mm});
            skLineSegment(sketch, "E286", {"start": v(57333.25, 52121.74) * mm, "end": v(57345.7, 52125.5) * mm});
            skLineSegment(sketch, "E287", {"start": v(57345.7, 52125.5) * mm, "end": v(57392.04, 51972.37) * mm});
            skLineSegment(sketch, "E288", {"start": v(57392.04, 51972.37) * mm, "end": v(57379.6, 51968.6) * mm});
            skLineSegment(sketch, "E289", {"start": v(57379.6, 51968.6) * mm, "end": v(57361.93, 52026.98) * mm});
            skArc(sketch, "E290", {"start": v(57361.93, 52026.98) * mm, "mid": v(57354.65, 52035.86) * mm, "end": v(57343.23, 52037) * mm});
            skLineSegment(sketch, "E291", {"start": v(57343.23, 52037) * mm, "end": v(57243.69, 52006.87) * mm});
            skArc(sketch, "E292", {"start": v(57243.69, 52006.87) * mm, "mid": v(57234.8, 51999.59) * mm, "end": v(57233.68, 51988.17) * mm});
            skLineSegment(sketch, "E293", {"start": v(57233.68, 51988.17) * mm, "end": v(57251.35, 51929.78) * mm});
            skCircle(sketch, "E294", {"center": v(57343, 51858.26) * mm, "radius": 10 * mm});
            skCircle(sketch, "E295", {"center": v(57124.8, 51975.06) * mm, "radius": 10 * mm});
            skCircle(sketch, "E296", {"center": v(57074.1, 52142.56) * mm, "radius": 10 * mm});
            skCircle(sketch, "E297", {"center": v(57175.5, 51807.57) * mm, "radius": 10 * mm});
            skCircle(sketch, "E298", {"center": v(57510.5, 51908.96) * mm, "radius": 10 * mm});
            skCircle(sketch, "E299", {"center": v(57409.1, 52243.95) * mm, "radius": 10 * mm});
            skCircle(sketch, "E300", {"center": v(57241.6, 52193.26) * mm, "radius": 10 * mm});
            skCircle(sketch, "E301", {"center": v(57459.8, 52076.46) * mm, "radius": 10 * mm});
            skLineSegment(sketch, "E302", {"start": v(57579.07, 51872.25) * mm, "end": v(57138.8, 51739) * mm});
            skLineSegment(sketch, "E303", {"start": v(57445.8, 52312.53) * mm, "end": v(57579.07, 51872.25) * mm});
            skLineSegment(sketch, "E304", {"start": v(57005.53, 52179.27) * mm, "end": v(57445.8, 52312.53) * mm});
            skLineSegment(sketch, "E305", {"start": v(57138.8, 51739) * mm, "end": v(57005.53, 52179.27) * mm});
            skLineSegment(sketch, "E306", {"start": v(54035.43, 50956.41) * mm, "end": v(54022.98, 50952.65) * mm});
            skLineSegment(sketch, "E307", {"start": v(54022.98, 50952.65) * mm, "end": v(53976.63, 51105.79) * mm});
            skLineSegment(sketch, "E308", {"start": v(53976.63, 51105.79) * mm, "end": v(53989.08, 51109.55) * mm});
            skLineSegment(sketch, "E309", {"start": v(53989.08, 51109.55) * mm, "end": v(54006.75, 51051.17) * mm});
            skArc(sketch, "E310", {"start": v(54006.75, 51051.17) * mm, "mid": v(54014.02, 51042.29) * mm, "end": v(54025.45, 51041.16) * mm});
            skLineSegment(sketch, "E311", {"start": v(54025.45, 51041.16) * mm, "end": v(54124.99, 51071.28) * mm});
            skArc(sketch, "E312", {"start": v(54124.99, 51071.28) * mm, "mid": v(54133.87, 51078.56) * mm, "end": v(54135, 51089.99) * mm});
            skLineSegment(sketch, "E313", {"start": v(54135, 51089.99) * mm, "end": v(54117.33, 51148.37) * mm});
            skLineSegment(sketch, "E314", {"start": v(54117.33, 51148.37) * mm, "end": v(54129.77, 51152.14) * mm});
            skLineSegment(sketch, "E315", {"start": v(54129.77, 51152.14) * mm, "end": v(54176.12, 50999) * mm});
            skLineSegment(sketch, "E316", {"start": v(54176.12, 50999) * mm, "end": v(54163.68, 50995.23) * mm});
            skLineSegment(sketch, "E317", {"start": v(54163.68, 50995.23) * mm, "end": v(54146, 51053.62) * mm});
            skArc(sketch, "E318", {"start": v(54146, 51053.62) * mm, "mid": v(54138.73, 51062.5) * mm, "end": v(54127.3, 51063.63) * mm});
            skLineSegment(sketch, "E319", {"start": v(54127.3, 51063.63) * mm, "end": v(54027.77, 51033.5) * mm});
            skArc(sketch, "E320", {"start": v(54027.77, 51033.5) * mm, "mid": v(54018.89, 51026.22) * mm, "end": v(54017.75, 51014.8) * mm});
            skLineSegment(sketch, "E321", {"start": v(54017.75, 51014.8) * mm, "end": v(54035.43, 50956.41) * mm});
            skCircle(sketch, "E322", {"center": v(54127.07, 50884.9) * mm, "radius": 10 * mm});
            skCircle(sketch, "E323", {"center": v(53908.88, 51001.7) * mm, "radius": 10 * mm});
            skCircle(sketch, "E324", {"center": v(53858.19, 51169.2) * mm, "radius": 10 * mm});
            skCircle(sketch, "E325", {"center": v(53959.58, 50834.2) * mm, "radius": 10 * mm});
            skCircle(sketch, "E326", {"center": v(54294.57, 50935.6) * mm, "radius": 10 * mm});
            skCircle(sketch, "E327", {"center": v(54193.18, 51270.58) * mm, "radius": 10 * mm});
            skCircle(sketch, "E328", {"center": v(54025.68, 51219.89) * mm, "radius": 10 * mm});
            skCircle(sketch, "E329", {"center": v(54243.87, 51103.09) * mm, "radius": 10 * mm});
            skLineSegment(sketch, "E330", {"start": v(54363.14, 50898.88) * mm, "end": v(53922.87, 50765.62) * mm});
            skLineSegment(sketch, "E331", {"start": v(54229.89, 51339.16) * mm, "end": v(54363.14, 50898.88) * mm});
            skLineSegment(sketch, "E332", {"start": v(53789.61, 51205.9) * mm, "end": v(54229.89, 51339.16) * mm});
            skLineSegment(sketch, "E333", {"start": v(53922.87, 50765.62) * mm, "end": v(53789.61, 51205.9) * mm});
            skLineSegment(sketch, "E334", {"start": v(52250.92, 56852.27) * mm, "end": v(52238.47, 56848.5) * mm});
            skLineSegment(sketch, "E335", {"start": v(52238.47, 56848.5) * mm, "end": v(52192.12, 57001.64) * mm});
            skLineSegment(sketch, "E336", {"start": v(52192.12, 57001.64) * mm, "end": v(52204.57, 57005.4) * mm});
            skLineSegment(sketch, "E337", {"start": v(52204.57, 57005.4) * mm, "end": v(52222.24, 56947.02) * mm});
            skArc(sketch, "E338", {"start": v(52222.24, 56947.02) * mm, "mid": v(52229.51, 56938.14) * mm, "end": v(52240.94, 56937.01) * mm});
            skLineSegment(sketch, "E339", {"start": v(52240.94, 56937.01) * mm, "end": v(52340.48, 56967.14) * mm});
            skArc(sketch, "E340", {"start": v(52340.48, 56967.14) * mm, "mid": v(52349.36, 56974.42) * mm, "end": v(52350.5, 56985.84) * mm});
            skLineSegment(sketch, "E341", {"start": v(52350.5, 56985.84) * mm, "end": v(52332.82, 57044.23) * mm});
            skLineSegment(sketch, "E342", {"start": v(52332.82, 57044.23) * mm, "end": v(52345.26, 57048) * mm});
            skLineSegment(sketch, "E343", {"start": v(52345.26, 57048) * mm, "end": v(52391.61, 56894.85) * mm});
            skLineSegment(sketch, "E344", {"start": v(52391.61, 56894.85) * mm, "end": v(52379.17, 56891.09) * mm});
            skLineSegment(sketch, "E345", {"start": v(52379.17, 56891.09) * mm, "end": v(52361.5, 56949.47) * mm});
            skArc(sketch, "E346", {"start": v(52361.5, 56949.47) * mm, "mid": v(52354.22, 56958.35) * mm, "end": v(52342.8, 56959.48) * mm});
            skLineSegment(sketch, "E347", {"start": v(52342.8, 56959.48) * mm, "end": v(52243.26, 56929.36) * mm});
            skArc(sketch, "E348", {"start": v(52243.26, 56929.36) * mm, "mid": v(52234.38, 56922.08) * mm, "end": v(52233.25, 56910.65) * mm});
            skLineSegment(sketch, "E349", {"start": v(52233.25, 56910.65) * mm, "end": v(52250.92, 56852.27) * mm});
            skCircle(sketch, "E350", {"center": v(52342.56, 56780.75) * mm, "radius": 10 * mm});
            skCircle(sketch, "E351", {"center": v(52124.37, 56897.55) * mm, "radius": 10 * mm});
            skCircle(sketch, "E352", {"center": v(52073.68, 57065.05) * mm, "radius": 10 * mm});
            skCircle(sketch, "E353", {"center": v(52175.07, 56730.06) * mm, "radius": 10 * mm});
            skCircle(sketch, "E354", {"center": v(52510.06, 56831.45) * mm, "radius": 10 * mm});
            skCircle(sketch, "E355", {"center": v(52408.67, 57166.44) * mm, "radius": 10 * mm});
            skCircle(sketch, "E356", {"center": v(52241.17, 57115.74) * mm, "radius": 10 * mm});
            skCircle(sketch, "E357", {"center": v(52459.36, 56998.94) * mm, "radius": 10 * mm});
            skLineSegment(sketch, "E358", {"start": v(52578.64, 56794.74) * mm, "end": v(52138.36, 56661.48) * mm});
            skLineSegment(sketch, "E359", {"start": v(52445.38, 57235.01) * mm, "end": v(52578.64, 56794.74) * mm});
            skLineSegment(sketch, "E360", {"start": v(52005.1, 57101.76) * mm, "end": v(52445.38, 57235.01) * mm});
            skLineSegment(sketch, "E361", {"start": v(52138.36, 56661.48) * mm, "end": v(52005.1, 57101.76) * mm});
            skLineSegment(sketch, "E362", {"start": v(55466.84, 57825.64) * mm, "end": v(55454.4, 57821.87) * mm});
            skLineSegment(sketch, "E363", {"start": v(55454.4, 57821.87) * mm, "end": v(55408.04, 57975.01) * mm});
            skLineSegment(sketch, "E364", {"start": v(55408.04, 57975.01) * mm, "end": v(55420.49, 57978.78) * mm});
            skLineSegment(sketch, "E365", {"start": v(55420.49, 57978.78) * mm, "end": v(55438.16, 57920.4) * mm});
            skArc(sketch, "E366", {"start": v(55438.16, 57920.4) * mm, "mid": v(55445.44, 57911.51) * mm, "end": v(55456.86, 57910.38) * mm});
            skLineSegment(sketch, "E367", {"start": v(55456.86, 57910.38) * mm, "end": v(55556.4, 57940.5) * mm});
            skArc(sketch, "E368", {"start": v(55556.4, 57940.5) * mm, "mid": v(55565.28, 57947.79) * mm, "end": v(55566.41, 57959.21) * mm});
            skLineSegment(sketch, "E369", {"start": v(55566.41, 57959.21) * mm, "end": v(55548.74, 58017.6) * mm});
            skLineSegment(sketch, "E370", {"start": v(55548.74, 58017.6) * mm, "end": v(55561.18, 58021.36) * mm});
            skLineSegment(sketch, "E371", {"start": v(55561.18, 58021.36) * mm, "end": v(55607.53, 57868.22) * mm});
            skLineSegment(sketch, "E372", {"start": v(55607.53, 57868.22) * mm, "end": v(55595.1, 57864.46) * mm});
            skLineSegment(sketch, "E373", {"start": v(55595.1, 57864.46) * mm, "end": v(55577.42, 57922.84) * mm});
            skArc(sketch, "E374", {"start": v(55577.42, 57922.84) * mm, "mid": v(55570.14, 57931.72) * mm, "end": v(55558.72, 57932.85) * mm});
            skLineSegment(sketch, "E375", {"start": v(55558.72, 57932.85) * mm, "end": v(55459.18, 57902.72) * mm});
            skArc(sketch, "E376", {"start": v(55459.18, 57902.72) * mm, "mid": v(55450.3, 57895.45) * mm, "end": v(55449.17, 57884.02) * mm});
            skLineSegment(sketch, "E377", {"start": v(55449.17, 57884.02) * mm, "end": v(55466.84, 57825.64) * mm});
            skCircle(sketch, "E378", {"center": v(55558.49, 57754.12) * mm, "radius": 10 * mm});
            skCircle(sketch, "E379", {"center": v(55340.3, 57870.92) * mm, "radius": 10 * mm});
            skCircle(sketch, "E380", {"center": v(55289.6, 58038.42) * mm, "radius": 10 * mm});
            skCircle(sketch, "E381", {"center": v(55391, 57703.42) * mm, "radius": 10 * mm});
            skCircle(sketch, "E382", {"center": v(55725.98, 57804.82) * mm, "radius": 10 * mm});
            skCircle(sketch, "E383", {"center": v(55624.59, 58139.8) * mm, "radius": 10 * mm});
            skCircle(sketch, "E384", {"center": v(55457.1, 58089.11) * mm, "radius": 10 * mm});
            skCircle(sketch, "E385", {"center": v(55675.29, 57972.31) * mm, "radius": 10 * mm});
            skLineSegment(sketch, "E386", {"start": v(55794.56, 57768.1) * mm, "end": v(55354.28, 57634.85) * mm});
            skLineSegment(sketch, "E387", {"start": v(55661.3, 58208.38) * mm, "end": v(55794.56, 57768.1) * mm});
            skLineSegment(sketch, "E388", {"start": v(55221.02, 58075.12) * mm, "end": v(55661.3, 58208.38) * mm});
            skLineSegment(sketch, "E389", {"start": v(55354.28, 57634.85) * mm, "end": v(55221.02, 58075.12) * mm});
            skLineSegment(sketch, "E390", {"start": v(54409.66, 51283.84) * mm, "end": v(52697.54, 56940.4) * mm});
            skLineSegment(sketch, "E391", {"start": v(52697.54, 56940.4) * mm, "end": v(55174.56, 57690.15) * mm});
            skLineSegment(sketch, "E392", {"start": v(55174.56, 57690.15) * mm, "end": v(56886.68, 52033.59) * mm});
            skLineSegment(sketch, "E393", {"start": v(56886.68, 52033.59) * mm, "end": v(54409.66, 51283.84) * mm});
            skLineSegment(sketch, "E394", {"start": v(39664.12, 55944.6) * mm, "end": v(40724.15, 52442.47) * mm});
            skLineSegment(sketch, "E395", {"start": v(38916.03, 56345.06) * mm, "end": v(39976, 52843.08) * mm});
            skLineSegment(sketch, "E396", {"start": v(40724.15, 52442.47) * mm, "end": v(36317.17, 51109.92) * mm});
            skLineSegment(sketch, "E397", {"start": v(39976, 52843.08) * mm, "end": v(36717.67, 51857.85) * mm});
            skLineSegment(sketch, "E398", {"start": v(30437.41, 72606.72) * mm, "end": v(36717.67, 51857.85) * mm});
            skLineSegment(sketch, "E399", {"start": v(29657.7, 73111.61) * mm, "end": v(36317.17, 51109.92) * mm});
            skLineSegment(sketch, "E400", {"start": v(38916.03, 56345.06) * mm, "end": v(44311.28, 57978.1) * mm});
            skLineSegment(sketch, "E401", {"start": v(44485.1, 57403.82) * mm, "end": v(44311.28, 57978.1) * mm});
            skLineSegment(sketch, "E402", {"start": v(39664.12, 55944.6) * mm, "end": v(44485.1, 57403.82) * mm});
            skLineSegment(sketch, "E403", {"start": v(29657.7, 73111.61) * mm, "end": v(53564.5, 76178.39) * mm});
            skLineSegment(sketch, "E404", {"start": v(30437.41, 72606.72) * mm, "end": v(53235.88, 75531.31) * mm});
            skLineSegment(sketch, "E405", {"start": v(68033.92, 49903.52) * mm, "end": v(54030.97, 45665.1) * mm});
            skLineSegment(sketch, "E406", {"start": v(67150.92, 50263.13) * mm, "end": v(54431.42, 46413.2) * mm});
            skLineSegment(sketch, "E407", {"start": v(54030.97, 45665.1) * mm, "end": v(49801.13, 59639.76) * mm});
            skLineSegment(sketch, "E408", {"start": v(50375.4, 59813.58) * mm, "end": v(49801.13, 59639.76) * mm});
            skLineSegment(sketch, "E409", {"start": v(54431.42, 46413.2) * mm, "end": v(50375.4, 59813.58) * mm});
            skLineSegment(sketch, "E410", {"start": v(53564.5, 76178.39) * mm, "end": v(68033.92, 49903.52) * mm});
            skLineSegment(sketch, "E411", {"start": v(53235.88, 75531.31) * mm, "end": v(67150.92, 50263.13) * mm});
            skLineSegment(sketch, "E412", {"start": v(43746.98, 61568.38) * mm, "end": v(39705.16, 60345.03) * mm});
            skLineSegment(sketch, "E413", {"start": v(39705.16, 60345.03) * mm, "end": v(39792.07, 60057.9) * mm});
            skLineSegment(sketch, "E414", {"start": v(39792.07, 60057.9) * mm, "end": v(43833.9, 61281.24) * mm});
            skLineSegment(sketch, "E415", {"start": v(43833.9, 61281.24) * mm, "end": v(43746.98, 61568.38) * mm});
            skLineSegment(sketch, "E416", {"start": v(41296.56, 69605.87) * mm, "end": v(42482.87, 61185.76) * mm});
            skLineSegment(sketch, "E417", {"start": v(48359.31, 61648.42) * mm, "end": v(47221.03, 70350.15) * mm});
            skLineSegment(sketch, "E418", {"start": v(46847.5, 70314.47) * mm, "end": v(47995.52, 61538.3) * mm});
            skLineSegment(sketch, "E419", {"start": v(55724.5, 60181.57) * mm, "end": v(50819.09, 58696.48) * mm});
            skLineSegment(sketch, "E420", {"start": v(49204.3, 59986.36) * mm, "end": v(54308.63, 61531.67) * mm});
            skLineSegment(sketch, "E421", {"start": v(48048.78, 64022.34) * mm, "end": v(52784.2, 65455.66) * mm});
            skLineSegment(sketch, "E422", {"start": v(52597.15, 65791.14) * mm, "end": v(47999.48, 64399.22) * mm});
            skLineSegment(sketch, "E423", {"start": v(54200, 61890.59) * mm, "end": v(49095.75, 60345.3) * mm});
            skLineSegment(sketch, "E424", {"start": v(32737.3, 66492.66) * mm, "end": v(35570.65, 67350.91) * mm});
            skLineSegment(sketch, "E425", {"start": v(37393.76, 61301.44) * mm, "end": v(35125.04, 68796.87) * mm});
            skLineSegment(sketch, "E426", {"start": v(37752.67, 61410.08) * mm, "end": v(35484.16, 68904.97) * mm});
            skLineSegment(sketch, "E427", {"start": v(32850.1, 66135) * mm, "end": v(35679.29, 66991.99) * mm});
            skLineSegment(sketch, "E428", {"start": v(59287.5, 52158.7) * mm, "end": v(60066.85, 52394.65) * mm});
            skLineSegment(sketch, "E429", {"start": v(57364.27, 55607.68) * mm, "end": v(58143.3, 55843.53) * mm});
            skLineSegment(sketch, "E430", {"start": v(41667.9, 69658.19) * mm, "end": v(42846.14, 61295.28) * mm});
            skLineSegment(sketch, "E431", {"start": v(37539.24, 62141.45) * mm, "end": v(41560.53, 67604.46) * mm});
            skLineSegment(sketch, "E432", {"start": v(41650.45, 67094.03) * mm, "end": v(37674.97, 61693.26) * mm});
            skLineSegment(sketch, "E433", {"start": v(31997.32, 72403.55) * mm, "end": v(33353.34, 67923.5) * mm});
            skLineSegment(sketch, "E434", {"start": v(40437.2, 70067.64) * mm, "end": v(39441.15, 73358.44) * mm});
            skLineSegment(sketch, "E435", {"start": v(33353.34, 67923.5) * mm, "end": v(40437.2, 70067.64) * mm});
            skLineSegment(sketch, "E436", {"start": v(38520.96, 69487.63) * mm, "end": v(38047.53, 73179.67) * mm});
            skLineSegment(sketch, "E437", {"start": v(38812.11, 69575.76) * mm, "end": v(38345.1, 73217.85) * mm});
            skLineSegment(sketch, "E438", {"start": v(35107.62, 70149.24) * mm, "end": v(34334.2, 72704.48) * mm});
            skLineSegment(sketch, "E439", {"start": v(34820.49, 70062.33) * mm, "end": v(34032.47, 72665.79) * mm});
            skLineSegment(sketch, "E440", {"start": v(35803.5, 68665.12) * mm, "end": v(35270.3, 72823.4) * mm});
            skLineSegment(sketch, "E441", {"start": v(36094.66, 68753.24) * mm, "end": v(35567.85, 72861.58) * mm});
            skLineSegment(sketch, "E442", {"start": v(39792.07, 60057.9) * mm, "end": v(38292.07, 59603.88) * mm});
            skLineSegment(sketch, "E443", {"start": v(39705.16, 60345.03) * mm, "end": v(38205.16, 59891.02) * mm});
            skLineSegment(sketch, "E444", {"start": v(48417.7, 61733.56) * mm, "end": v(53758.17, 63350.02) * mm});
            skLineSegment(sketch, "E445", {"start": v(48798.71, 61326.49) * mm, "end": v(53903.04, 62871.46) * mm});
            skLineSegment(sketch, "E446", {"start": v(35125.2, 68796.33) * mm, "end": v(35484.16, 68904.97) * mm});
            skLineSegment(sketch, "E447", {"start": v(37391.17, 61300.66) * mm, "end": v(37750.12, 61409.3) * mm});
            skLineSegment(sketch, "E448", {"start": v(64765.56, 53744.58) * mm, "end": v(64866.07, 53800.47) * mm});
            skLineSegment(sketch, "E449", {"start": v(64866.07, 53800.47) * mm, "end": v(65157.68, 53276.1) * mm});
            skLineSegment(sketch, "E450", {"start": v(65157.68, 53276.1) * mm, "end": v(65057.18, 53220.21) * mm});
            skLineSegment(sketch, "E451", {"start": v(65057.18, 53220.21) * mm, "end": v(64765.56, 53744.58) * mm});
            skLineSegment(sketch, "E452", {"start": v(30437.41, 72606.72) * mm, "end": v(53075.2, 75510.7) * mm});
            skLineSegment(sketch, "E453", {"start": v(30957.21, 72270.12) * mm, "end": v(52857.63, 75079.51) * mm});
            skLineSegment(sketch, "E454", {"start": v(53075.2, 75510.7) * mm, "end": v(67150.92, 50263.13) * mm});
            skLineSegment(sketch, "E455", {"start": v(52857.63, 75079.51) * mm, "end": v(66559.72, 50502.1) * mm});
            skLineSegment(sketch, "E456", {"start": v(67150.92, 50263.13) * mm, "end": v(54145.32, 46326.6) * mm});
            skLineSegment(sketch, "E457", {"start": v(66559.72, 50502.1) * mm, "end": v(54412.29, 46825.33) * mm});
            skLineSegment(sketch, "E458", {"start": v(54145.32, 46326.6) * mm, "end": v(50089.3, 59726.98) * mm});
            skLineSegment(sketch, "E459", {"start": v(54412.29, 46825.33) * mm, "end": v(50356.27, 60225.7) * mm});
            skLineSegment(sketch, "E460", {"start": v(50089.3, 59726.98) * mm, "end": v(49336.06, 59499) * mm});
            skLineSegment(sketch, "E461", {"start": v(49220.18, 59881.84) * mm, "end": v(49336.06, 59499) * mm});
            skLineSegment(sketch, "E462", {"start": v(50356.27, 60225.7) * mm, "end": v(49220.18, 59881.84) * mm});
            skLineSegment(sketch, "E463", {"start": v(39517.02, 53123.18) * mm, "end": v(38573.23, 56241.3) * mm});
            skLineSegment(sketch, "E464", {"start": v(39977.46, 52844.63) * mm, "end": v(38917.8, 56345.6) * mm});
            skLineSegment(sketch, "E465", {"start": v(35924.94, 55857.64) * mm, "end": v(44386.82, 58418.88) * mm});
            skLineSegment(sketch, "E466", {"start": v(44502.7, 58036.03) * mm, "end": v(44386.82, 58418.88) * mm});
            skLineSegment(sketch, "E467", {"start": v(38917.8, 56345.6) * mm, "end": v(44502.7, 58036.03) * mm});
            skLineSegment(sketch, "E468", {"start": v(36040.82, 55474.8) * mm, "end": v(38573.23, 56241.3) * mm});
            skLineSegment(sketch, "E469", {"start": v(30957.21, 72270.12) * mm, "end": v(36984.61, 52356.67) * mm});
            skLineSegment(sketch, "E470", {"start": v(36040.82, 55474.8) * mm, "end": v(36984.61, 52356.67) * mm});
            skLineSegment(sketch, "E471", {"start": v(30437.41, 72606.72) * mm, "end": v(36717.64, 51857.95) * mm});
            skLineSegment(sketch, "E472", {"start": v(30957.21, 72270.12) * mm, "end": v(35924.94, 55857.64) * mm});
            skLineSegment(sketch, "E473", {"start": v(36984.61, 52356.67) * mm, "end": v(39517.02, 53123.18) * mm});
            skLineSegment(sketch, "E474", {"start": v(36717.64, 51857.95) * mm, "end": v(39977.46, 52844.63) * mm});
            skCircle(sketch, "E475", {"center": v(53400.19, 75854.85) * mm, "radius": 300 * mm});
            skLineSegment(sketch, "E476", {"start": v(53400.19, 75854.85) * mm, "end": v(67780.92, 49741.01) * mm});
            skCircle(sketch, "E477", {"center": v(53759.7, 75202) * mm, "radius": 300 * mm});
            skCircle(sketch, "E478", {"center": v(54119.23, 74549.16) * mm, "radius": 300 * mm});
            skCircle(sketch, "E479", {"center": v(54478.74, 73896.31) * mm, "radius": 300 * mm});
            skCircle(sketch, "E480", {"center": v(54838.26, 73243.47) * mm, "radius": 300 * mm});
            skCircle(sketch, "E481", {"center": v(55197.78, 72590.62) * mm, "radius": 300 * mm});
            skCircle(sketch, "E482", {"center": v(55557.3, 71937.77) * mm, "radius": 300 * mm});
            skCircle(sketch, "E483", {"center": v(55916.82, 71284.93) * mm, "radius": 300 * mm});
            skCircle(sketch, "E484", {"center": v(56276.34, 70632.08) * mm, "radius": 300 * mm});
            skCircle(sketch, "E485", {"center": v(56635.85, 69979.24) * mm, "radius": 300 * mm});
            skCircle(sketch, "E486", {"center": v(56995.37, 69326.4) * mm, "radius": 300 * mm});
            skCircle(sketch, "E487", {"center": v(57354.9, 68673.55) * mm, "radius": 300 * mm});
            skCircle(sketch, "E488", {"center": v(57714.4, 68020.7) * mm, "radius": 300 * mm});
            skCircle(sketch, "E489", {"center": v(58073.93, 67367.85) * mm, "radius": 300 * mm});
            skCircle(sketch, "E490", {"center": v(58433.45, 66715) * mm, "radius": 300 * mm});
            skCircle(sketch, "E491", {"center": v(58792.97, 66062.16) * mm, "radius": 300 * mm});
            skCircle(sketch, "E492", {"center": v(59152.48, 65409.32) * mm, "radius": 300 * mm});
            skCircle(sketch, "E493", {"center": v(59512, 64756.47) * mm, "radius": 300 * mm});
            skCircle(sketch, "E494", {"center": v(59871.52, 64103.62) * mm, "radius": 300 * mm});
            skCircle(sketch, "E495", {"center": v(60231.04, 63450.78) * mm, "radius": 300 * mm});
            skCircle(sketch, "E496", {"center": v(60590.56, 62797.93) * mm, "radius": 300 * mm});
            skCircle(sketch, "E497", {"center": v(60950.08, 62145.09) * mm, "radius": 300 * mm});
            skCircle(sketch, "E498", {"center": v(61309.6, 61492.24) * mm, "radius": 300 * mm});
            skCircle(sketch, "E499", {"center": v(61669.11, 60839.4) * mm, "radius": 300 * mm});
            skCircle(sketch, "E500", {"center": v(62028.63, 60186.55) * mm, "radius": 300 * mm});
            skCircle(sketch, "E501", {"center": v(62388.15, 59533.7) * mm, "radius": 300 * mm});
            skCircle(sketch, "E502", {"center": v(62747.67, 58880.86) * mm, "radius": 300 * mm});
            skCircle(sketch, "E503", {"center": v(63107.19, 58228.01) * mm, "radius": 300 * mm});
            skCircle(sketch, "E504", {"center": v(63466.7, 57575.16) * mm, "radius": 300 * mm});
            skCircle(sketch, "E505", {"center": v(63826.22, 56922.32) * mm, "radius": 300 * mm});
            skCircle(sketch, "E506", {"center": v(64185.74, 56269.47) * mm, "radius": 300 * mm});
            skCircle(sketch, "E507", {"center": v(64545.26, 55616.63) * mm, "radius": 300 * mm});
            skCircle(sketch, "E508", {"center": v(64904.78, 54963.78) * mm, "radius": 300 * mm});
            skCircle(sketch, "E509", {"center": v(65264.3, 54310.94) * mm, "radius": 300 * mm});
            skCircle(sketch, "E510", {"center": v(65623.81, 53658.09) * mm, "radius": 300 * mm});
            skCircle(sketch, "E511", {"center": v(65983.33, 53005.24) * mm, "radius": 300 * mm});
            skCircle(sketch, "E512", {"center": v(66342.85, 52352.4) * mm, "radius": 300 * mm});
            skCircle(sketch, "E513", {"center": v(66702.37, 51699.55) * mm, "radius": 300 * mm});
            skCircle(sketch, "E514", {"center": v(67061.89, 51046.7) * mm, "radius": 300 * mm});
            skCircle(sketch, "E515", {"center": v(67421.4, 50393.86) * mm, "radius": 300 * mm});
            skCircle(sketch, "E516", {"center": v(67824.74, 49764.95) * mm, "radius": 300 * mm});
            skCircle(sketch, "E517", {"center": v(53939.47, 74875.58) * mm, "radius": 300 * mm});
            skCircle(sketch, "E518", {"center": v(54298.99, 74222.74) * mm, "radius": 300 * mm});
            skCircle(sketch, "E519", {"center": v(54658.5, 73569.89) * mm, "radius": 300 * mm});
            skCircle(sketch, "E520", {"center": v(55018.02, 72917.04) * mm, "radius": 300 * mm});
            skCircle(sketch, "E521", {"center": v(55377.54, 72264.2) * mm, "radius": 300 * mm});
            skCircle(sketch, "E522", {"center": v(55737.06, 71611.35) * mm, "radius": 300 * mm});
            skCircle(sketch, "E523", {"center": v(56096.58, 70958.5) * mm, "radius": 300 * mm});
            skCircle(sketch, "E524", {"center": v(56456.1, 70305.66) * mm, "radius": 300 * mm});
            skCircle(sketch, "E525", {"center": v(56815.61, 69652.81) * mm, "radius": 300 * mm});
            skCircle(sketch, "E526", {"center": v(57175.13, 68999.97) * mm, "radius": 300 * mm});
            skCircle(sketch, "E527", {"center": v(57534.65, 68347.12) * mm, "radius": 300 * mm});
            skCircle(sketch, "E528", {"center": v(57894.17, 67694.28) * mm, "radius": 300 * mm});
            skCircle(sketch, "E529", {"center": v(58253.69, 67041.43) * mm, "radius": 300 * mm});
            skCircle(sketch, "E530", {"center": v(58613.2, 66388.58) * mm, "radius": 300 * mm});
            skCircle(sketch, "E531", {"center": v(58972.72, 65735.74) * mm, "radius": 300 * mm});
            skCircle(sketch, "E532", {"center": v(59332.24, 65082.9) * mm, "radius": 300 * mm});
            skCircle(sketch, "E533", {"center": v(59691.76, 64430.05) * mm, "radius": 300 * mm});
            skCircle(sketch, "E534", {"center": v(60051.28, 63777.2) * mm, "radius": 300 * mm});
            skCircle(sketch, "E535", {"center": v(60410.8, 63124.35) * mm, "radius": 300 * mm});
            skCircle(sketch, "E536", {"center": v(60770.32, 62471.5) * mm, "radius": 300 * mm});
            skCircle(sketch, "E537", {"center": v(61129.83, 61818.66) * mm, "radius": 300 * mm});
            skCircle(sketch, "E538", {"center": v(61489.35, 61165.82) * mm, "radius": 300 * mm});
            skCircle(sketch, "E539", {"center": v(61848.87, 60512.97) * mm, "radius": 300 * mm});
            skCircle(sketch, "E540", {"center": v(62208.39, 59860.13) * mm, "radius": 300 * mm});
            skCircle(sketch, "E541", {"center": v(62567.9, 59207.28) * mm, "radius": 300 * mm});
            skCircle(sketch, "E542", {"center": v(62927.43, 58554.43) * mm, "radius": 300 * mm});
            skCircle(sketch, "E543", {"center": v(63286.94, 57901.59) * mm, "radius": 300 * mm});
            skCircle(sketch, "E544", {"center": v(63646.46, 57248.74) * mm, "radius": 300 * mm});
            skCircle(sketch, "E545", {"center": v(64005.98, 56595.9) * mm, "radius": 300 * mm});
            skCircle(sketch, "E546", {"center": v(64725.02, 55290.2) * mm, "radius": 300 * mm});
            skCircle(sketch, "E547", {"center": v(65084.54, 54637.36) * mm, "radius": 300 * mm});
            skCircle(sketch, "E548", {"center": v(65444.05, 53984.51) * mm, "radius": 300 * mm});
            skCircle(sketch, "E549", {"center": v(64365.5, 55943.05) * mm, "radius": 300 * mm});
            skCircle(sketch, "E550", {"center": v(65803.57, 53331.67) * mm, "radius": 300 * mm});
            skCircle(sketch, "E551", {"center": v(66163.1, 52678.82) * mm, "radius": 300 * mm});
            skCircle(sketch, "E552", {"center": v(66882.13, 51373.13) * mm, "radius": 300 * mm});
            skCircle(sketch, "E553", {"center": v(67241.65, 50720.28) * mm, "radius": 300 * mm});
            skCircle(sketch, "E554", {"center": v(66522.61, 52025.97) * mm, "radius": 300 * mm});
            skCircle(sketch, "E555", {"center": v(49888.89, 59352.88) * mm, "radius": 300 * mm});
            skCircle(sketch, "E556", {"center": v(53945.1, 45952.56) * mm, "radius": 300 * mm});
            skCircle(sketch, "E557", {"center": v(30047.42, 72859.15) * mm, "radius": 300 * mm});
            skCircle(sketch, "E558", {"center": v(33293.56, 62134.5) * mm, "radius": 300 * mm});
            skCircle(sketch, "E559", {"center": v(33077.15, 62849.46) * mm, "radius": 300 * mm});
            skCircle(sketch, "E560", {"center": v(32860.74, 63564.43) * mm, "radius": 300 * mm});
            skCircle(sketch, "E561", {"center": v(32644.34, 64279.4) * mm, "radius": 300 * mm});
            skCircle(sketch, "E562", {"center": v(32427.93, 64994.36) * mm, "radius": 300 * mm});
            skCircle(sketch, "E563", {"center": v(32211.53, 65709.33) * mm, "radius": 300 * mm});
            skCircle(sketch, "E564", {"center": v(31995.12, 66424.3) * mm, "radius": 300 * mm});
            skCircle(sketch, "E565", {"center": v(31778.71, 67139.26) * mm, "radius": 300 * mm});
            skCircle(sketch, "E566", {"center": v(31562.3, 67854.23) * mm, "radius": 300 * mm});
            skCircle(sketch, "E567", {"center": v(31345.9, 68569.2) * mm, "radius": 300 * mm});
            skCircle(sketch, "E568", {"center": v(31129.5, 69284.16) * mm, "radius": 300 * mm});
            skCircle(sketch, "E569", {"center": v(30913.1, 69999.13) * mm, "radius": 300 * mm});
            skCircle(sketch, "E570", {"center": v(30696.68, 70714.1) * mm, "radius": 300 * mm});
            skCircle(sketch, "E571", {"center": v(30480.28, 71429.06) * mm, "radius": 300 * mm});
            skCircle(sketch, "E572", {"center": v(30263.87, 72144.03) * mm, "radius": 300 * mm});
            skCircle(sketch, "E573", {"center": v(30777.44, 72952.8) * mm, "radius": 300 * mm});
            skCircle(sketch, "E574", {"center": v(31507.46, 73046.44) * mm, "radius": 300 * mm});
            skCircle(sketch, "E575", {"center": v(32237.47, 73140.09) * mm, "radius": 300 * mm});
            skCircle(sketch, "E576", {"center": v(32967.5, 73233.74) * mm, "radius": 300 * mm});
            skCircle(sketch, "E577", {"center": v(33697.51, 73327.38) * mm, "radius": 300 * mm});
            skCircle(sketch, "E578", {"center": v(34427.53, 73421.03) * mm, "radius": 300 * mm});
            skCircle(sketch, "E579", {"center": v(35157.55, 73514.68) * mm, "radius": 300 * mm});
            skCircle(sketch, "E580", {"center": v(35887.56, 73608.32) * mm, "radius": 300 * mm});
            skCircle(sketch, "E581", {"center": v(36617.58, 73701.97) * mm, "radius": 300 * mm});
            skCircle(sketch, "E582", {"center": v(37347.6, 73795.62) * mm, "radius": 300 * mm});
            skCircle(sketch, "E583", {"center": v(38077.62, 73889.27) * mm, "radius": 300 * mm});
            skCircle(sketch, "E584", {"center": v(38807.64, 73982.91) * mm, "radius": 300 * mm});
            skCircle(sketch, "E585", {"center": v(39537.65, 74076.56) * mm, "radius": 300 * mm});
            skCircle(sketch, "E586", {"center": v(40267.67, 74170.2) * mm, "radius": 300 * mm});
            skCircle(sketch, "E587", {"center": v(40997.7, 74263.85) * mm, "radius": 300 * mm});
            skCircle(sketch, "E588", {"center": v(41727.7, 74357.5) * mm, "radius": 300 * mm});
            skCircle(sketch, "E589", {"center": v(42457.73, 74451.15) * mm, "radius": 300 * mm});
            skCircle(sketch, "E590", {"center": v(43187.74, 74544.8) * mm, "radius": 300 * mm});
            skCircle(sketch, "E591", {"center": v(43917.76, 74638.44) * mm, "radius": 300 * mm});
            skCircle(sketch, "E592", {"center": v(44647.78, 74732.09) * mm, "radius": 300 * mm});
            skCircle(sketch, "E593", {"center": v(45377.8, 74825.74) * mm, "radius": 300 * mm});
            skCircle(sketch, "E594", {"center": v(46107.82, 74919.38) * mm, "radius": 300 * mm});
            skCircle(sketch, "E595", {"center": v(46837.83, 75013.03) * mm, "radius": 300 * mm});
            skCircle(sketch, "E596", {"center": v(47567.85, 75106.68) * mm, "radius": 300 * mm});
            skCircle(sketch, "E597", {"center": v(48297.87, 75200.32) * mm, "radius": 300 * mm});
            skCircle(sketch, "E598", {"center": v(49027.89, 75293.97) * mm, "radius": 300 * mm});
            skCircle(sketch, "E599", {"center": v(49757.9, 75387.62) * mm, "radius": 300 * mm});
            skCircle(sketch, "E600", {"center": v(50487.92, 75481.26) * mm, "radius": 300 * mm});
            skCircle(sketch, "E601", {"center": v(51217.94, 75574.91) * mm, "radius": 300 * mm});
            skCircle(sketch, "E602", {"center": v(51947.96, 75668.56) * mm, "radius": 300 * mm});
            skCircle(sketch, "E603", {"center": v(52677.98, 75762.2) * mm, "radius": 300 * mm});
            skCircle(sketch, "E604", {"center": v(54664.85, 46170.41) * mm, "radius": 300 * mm});
            skCircle(sketch, "E605", {"center": v(55384.6, 46388.28) * mm, "radius": 300 * mm});
            skCircle(sketch, "E606", {"center": v(56104.35, 46606.14) * mm, "radius": 300 * mm});
            skCircle(sketch, "E607", {"center": v(56824.1, 46824) * mm, "radius": 300 * mm});
            skCircle(sketch, "E608", {"center": v(57543.85, 47041.87) * mm, "radius": 300 * mm});
            skCircle(sketch, "E609", {"center": v(58263.6, 47259.73) * mm, "radius": 300 * mm});
            skCircle(sketch, "E610", {"center": v(58983.35, 47477.6) * mm, "radius": 300 * mm});
            skCircle(sketch, "E611", {"center": v(59703.1, 47695.46) * mm, "radius": 300 * mm});
            skCircle(sketch, "E612", {"center": v(60422.84, 47913.33) * mm, "radius": 300 * mm});
            skCircle(sketch, "E613", {"center": v(61142.6, 48131.2) * mm, "radius": 300 * mm});
            skCircle(sketch, "E614", {"center": v(61862.34, 48349.06) * mm, "radius": 300 * mm});
            skCircle(sketch, "E615", {"center": v(62582.1, 48566.92) * mm, "radius": 300 * mm});
            skCircle(sketch, "E616", {"center": v(63301.84, 48784.78) * mm, "radius": 300 * mm});
            skCircle(sketch, "E617", {"center": v(64021.6, 49002.65) * mm, "radius": 300 * mm});
            skCircle(sketch, "E618", {"center": v(64741.34, 49220.51) * mm, "radius": 300 * mm});
            skCircle(sketch, "E619", {"center": v(65461.09, 49438.38) * mm, "radius": 300 * mm});
            skCircle(sketch, "E620", {"center": v(66180.84, 49656.24) * mm, "radius": 300 * mm});
            skCircle(sketch, "E621", {"center": v(53731.58, 46657.95) * mm, "radius": 300 * mm});
            skCircle(sketch, "E622", {"center": v(53518.06, 47363.34) * mm, "radius": 300 * mm});
            skCircle(sketch, "E623", {"center": v(53304.54, 48068.73) * mm, "radius": 300 * mm});
            skCircle(sketch, "E624", {"center": v(53091.02, 48774.13) * mm, "radius": 300 * mm});
            skCircle(sketch, "E625", {"center": v(52877.5, 49479.52) * mm, "radius": 300 * mm});
            skCircle(sketch, "E626", {"center": v(52663.99, 50184.91) * mm, "radius": 300 * mm});
            skCircle(sketch, "E627", {"center": v(52450.47, 50890.3) * mm, "radius": 300 * mm});
            skCircle(sketch, "E628", {"center": v(52236.95, 51595.7) * mm, "radius": 300 * mm});
            skCircle(sketch, "E629", {"center": v(52023.43, 52301.1) * mm, "radius": 300 * mm});
            skCircle(sketch, "E630", {"center": v(51809.91, 53006.48) * mm, "radius": 300 * mm});
            skCircle(sketch, "E631", {"center": v(51596.4, 53711.88) * mm, "radius": 300 * mm});
            skCircle(sketch, "E632", {"center": v(51382.87, 54417.27) * mm, "radius": 300 * mm});
            skCircle(sketch, "E633", {"center": v(51169.35, 55122.66) * mm, "radius": 300 * mm});
            skCircle(sketch, "E634", {"center": v(50955.84, 55828.05) * mm, "radius": 300 * mm});
            skCircle(sketch, "E635", {"center": v(50742.32, 56533.45) * mm, "radius": 300 * mm});
            skCircle(sketch, "E636", {"center": v(50528.8, 57238.84) * mm, "radius": 300 * mm});
            skCircle(sketch, "E637", {"center": v(50315.28, 57944.23) * mm, "radius": 300 * mm});
            skCircle(sketch, "E638", {"center": v(50101.76, 58649.62) * mm, "radius": 300 * mm});
            skLineSegment(sketch, "E639", {"start": v(30047.42, 72859.15) * mm, "end": v(35457.62, 54984.83) * mm});
            skLineSegment(sketch, "E640", {"start": v(53945.1, 45952.56) * mm, "end": v(49888.89, 59352.88) * mm});
            skLineSegment(sketch, "E641", {"start": v(53945.1, 45952.56) * mm, "end": v(66900.59, 49874.1) * mm});
            skLineSegment(sketch, "E642", {"start": v(30047.42, 72859.15) * mm, "end": v(53400.19, 75854.85) * mm});
            skCircle(sketch, "E643", {"center": v(53579.95, 75528.43) * mm, "radius": 300 * mm});
            skCircle(sketch, "E644", {"center": v(40161.14, 53266.98) * mm, "radius": 300 * mm});
            skCircle(sketch, "E645", {"center": v(39509.32, 55420.5) * mm, "radius": 300 * mm});
            skCircle(sketch, "E646", {"center": v(39726.6, 54702.66) * mm, "radius": 300 * mm});
            skCircle(sketch, "E647", {"center": v(39943.87, 53984.82) * mm, "radius": 300 * mm});
            skCircle(sketch, "E648", {"center": v(44086.3, 57596.56) * mm, "radius": 300 * mm});
            skCircle(sketch, "E649", {"center": v(42647.96, 57161.2) * mm, "radius": 300 * mm});
            skCircle(sketch, "E650", {"center": v(43367, 57378.84) * mm, "radius": 300 * mm});
            skCircle(sketch, "E651", {"center": v(33483.8, 61505.57) * mm, "radius": 300 * mm});
            skLineSegment(sketch, "E652", {"start": v(40350.08, 52642.78) * mm, "end": v(39290.08, 56144.84) * mm});
            skLineSegment(sketch, "E653", {"start": v(36517.3, 51483.84) * mm, "end": v(35457.62, 54984.83) * mm});
            skCircle(sketch, "E654", {"center": v(33621.22, 60726.77) * mm, "radius": 375 * mm});
            skLineSegment(sketch, "E655", {"start": v(35123.8, 56106.32) * mm, "end": v(35600.08, 54499.8) * mm});
            skLineSegment(sketch, "E656", {"start": v(34931.23, 56052.24) * mm, "end": v(35408.33, 54442.95) * mm});
            skLineSegment(sketch, "E657", {"start": v(34713.87, 57650.93) * mm, "end": v(35123.8, 56106.32) * mm});
            skLineSegment(sketch, "E658", {"start": v(34522.07, 57593.97) * mm, "end": v(34931.23, 56052.24) * mm});
            skLineSegment(sketch, "E659", {"start": v(34069.7, 59608.22) * mm, "end": v(34713.87, 57650.93) * mm});
            skLineSegment(sketch, "E660", {"start": v(33879.73, 59545.7) * mm, "end": v(34522.07, 57593.97) * mm});
            skLineSegment(sketch, "E661", {"start": v(33879.73, 59545.7) * mm, "end": v(34069.7, 59608.22) * mm});
            skCircle(sketch, "E662", {"center": v(35503.23, 54471.13) * mm, "radius": 375 * mm});
            skCircle(sketch, "E663", {"center": v(35024.65, 56078.4) * mm, "radius": 375 * mm});
            skCircle(sketch, "E664", {"center": v(34617.97, 57622.45) * mm, "radius": 300 * mm});
            skCircle(sketch, "E665", {"center": v(33974.72, 59576.96) * mm, "radius": 375 * mm});
            skCircle(sketch, "E666", {"center": v(35948.4, 52971.91) * mm, "radius": 375 * mm});
            skCircle(sketch, "E667", {"center": v(36387.31, 51517) * mm, "radius": 375 * mm});
            skCircle(sketch, "E668", {"center": v(37796.6, 51792.76) * mm, "radius": 375 * mm});
            skCircle(sketch, "E669", {"center": v(39835.27, 56332.54) * mm, "radius": 375 * mm});
            skCircle(sketch, "E670", {"center": v(41846.6, 56950.07) * mm, "radius": 375 * mm});
            skLineSegment(sketch, "E671", {"start": v(35706.21, 54140.42) * mm, "end": v(35937.9, 53360.17) * mm});
            skLineSegment(sketch, "E672", {"start": v(35746.17, 53303.24) * mm, "end": v(35937.9, 53360.17) * mm});
            skLineSegment(sketch, "E673", {"start": v(35514.49, 54083.49) * mm, "end": v(35746.17, 53303.24) * mm});
            skLineSegment(sketch, "E674", {"start": v(35514.49, 54083.49) * mm, "end": v(35706.21, 54140.42) * mm});
            skLineSegment(sketch, "E675", {"start": v(36152.82, 52642.08) * mm, "end": v(36375.12, 51905.21) * mm});
            skLineSegment(sketch, "E676", {"start": v(36183.64, 51847.45) * mm, "end": v(36375.12, 51905.21) * mm});
            skLineSegment(sketch, "E677", {"start": v(35961.34, 52584.32) * mm, "end": v(36183.64, 51847.45) * mm});
            skLineSegment(sketch, "E678", {"start": v(35961.34, 52584.32) * mm, "end": v(36152.82, 52642.08) * mm});
            skLineSegment(sketch, "E679", {"start": v(36736.53, 51687.4) * mm, "end": v(37409.39, 51818.95) * mm});
            skLineSegment(sketch, "E680", {"start": v(37447.76, 51622.67) * mm, "end": v(37409.39, 51818.95) * mm});
            skLineSegment(sketch, "E681", {"start": v(36774.9, 51491.12) * mm, "end": v(37447.76, 51622.67) * mm});
            skLineSegment(sketch, "E682", {"start": v(36774.9, 51491.12) * mm, "end": v(36736.53, 51687.4) * mm});
            skLineSegment(sketch, "E683", {"start": v(40164.4, 56538.2) * mm, "end": v(41458.77, 56935.6) * mm});
            skLineSegment(sketch, "E684", {"start": v(41517.47, 56744.4) * mm, "end": v(41458.77, 56935.6) * mm});
            skLineSegment(sketch, "E685", {"start": v(40223.1, 56347) * mm, "end": v(41517.47, 56744.4) * mm});
            skLineSegment(sketch, "E686", {"start": v(40223.1, 56347) * mm, "end": v(40164.4, 56538.2) * mm});
            skCircle(sketch, "E687", {"center": v(38530.81, 52093.36) * mm, "radius": 300 * mm});
            skCircle(sketch, "E688", {"center": v(39248.7, 52310.48) * mm, "radius": 300 * mm});
            skCircle(sketch, "E689", {"center": v(39966.5, 52527.84) * mm, "radius": 300 * mm});
            skLineSegment(sketch, "E690", {"start": v(36517.4, 51483.94) * mm, "end": v(40348.6, 52643.57) * mm});
            skLineSegment(sketch, "E691", {"start": v(39290.08, 56144.84) * mm, "end": v(44398.2, 57690.92) * mm});
            skCircle(sketch, "E692", {"center": v(67171.9, 49625.85) * mm, "radius": 300 * mm});
            skLineSegment(sketch, "E693", {"start": v(43459.74, 61481.43) * mm, "end": v(43746.88, 61568.34) * mm});
            skLineSegment(sketch, "E694", {"start": v(43746.88, 61568.34) * mm, "end": v(43833.79, 61281.2) * mm});
            skLineSegment(sketch, "E695", {"start": v(43833.79, 61281.2) * mm, "end": v(43546.65, 61194.3) * mm});
            skLineSegment(sketch, "E696", {"start": v(43546.65, 61194.3) * mm, "end": v(43459.74, 61481.43) * mm});
            skLineSegment(sketch, "E697", {"start": v(43546.65, 61194.3) * mm, "end": v(43824.77, 60275.46) * mm});
            skLineSegment(sketch, "E698", {"start": v(43833.79, 61281.2) * mm, "end": v(44112, 60362.4) * mm});
            skLineSegment(sketch, "E699", {"start": v(49601.8, 74661.76) * mm, "end": v(50131.26, 70514.15) * mm});
            skLineSegment(sketch, "E700", {"start": v(49304.21, 74623.77) * mm, "end": v(49909.66, 69880.9) * mm});
            skLineSegment(sketch, "E701", {"start": v(49304.21, 74623.77) * mm, "end": v(49601.8, 74661.76) * mm});
            skLineSegment(sketch, "E702", {"start": v(47015.81, 71647.18) * mm, "end": v(47180.44, 70357.55) * mm});
            skLineSegment(sketch, "E703", {"start": v(46882.85, 70319.56) * mm, "end": v(47180.44, 70357.55) * mm});
            skLineSegment(sketch, "E704", {"start": v(46718.23, 71609.2) * mm, "end": v(46882.85, 70319.56) * mm});
            skLineSegment(sketch, "E705", {"start": v(46718.23, 71609.2) * mm, "end": v(47015.81, 71647.18) * mm});
            skLineSegment(sketch, "E706", {"start": v(41460.6, 70937.97) * mm, "end": v(41625.98, 69648.52) * mm});
            skLineSegment(sketch, "E707", {"start": v(41328.42, 69610.36) * mm, "end": v(41625.98, 69648.52) * mm});
            skLineSegment(sketch, "E708", {"start": v(41163.04, 70899.8) * mm, "end": v(41328.42, 69610.36) * mm});
            skLineSegment(sketch, "E709", {"start": v(41163.04, 70899.8) * mm, "end": v(41460.6, 70937.97) * mm});
            skLineSegment(sketch, "E710", {"start": v(38209.1, 59892.17) * mm, "end": v(43746.98, 61568.38) * mm});
            skLineSegment(sketch, "E711", {"start": v(42856.08, 61298.72) * mm, "end": v(43746.98, 61568.38) * mm});
            skLineSegment(sketch, "E712", {"start": v(38296.02, 59605.04) * mm, "end": v(43833.9, 61281.24) * mm});
            skLineSegment(sketch, "E713", {"start": v(38209.1, 59892.17) * mm, "end": v(42377.52, 61153.87) * mm});
            skLineSegment(sketch, "E714", {"start": v(37749.93, 61409.25) * mm, "end": v(39136.07, 56829.58) * mm});
            skLineSegment(sketch, "E715", {"start": v(38296.02, 59605.04) * mm, "end": v(39136.07, 56829.58) * mm});
            skLineSegment(sketch, "E716", {"start": v(37462.8, 61322.34) * mm, "end": v(38848.93, 56742.67) * mm});
            skLineSegment(sketch, "E717", {"start": v(37749.93, 61409.25) * mm, "end": v(38209.1, 59892.17) * mm});
            skLineSegment(sketch, "E718", {"start": v(56060.35, 60596.37) * mm, "end": v(56498.65, 59810.3) * mm});
            skLineSegment(sketch, "E719", {"start": v(56192.96, 59639.86) * mm, "end": v(56498.65, 59810.3) * mm});
            skLineSegment(sketch, "E720", {"start": v(55754.66, 60425.92) * mm, "end": v(56192.96, 59639.86) * mm});
            skLineSegment(sketch, "E721", {"start": v(55754.66, 60425.92) * mm, "end": v(56060.35, 60596.37) * mm});
            skLineSegment(sketch, "E722", {"start": v(43746.88, 61568.34) * mm, "end": v(43459.74, 61481.43) * mm});
            skLineSegment(sketch, "E723", {"start": v(43833.79, 61281.2) * mm, "end": v(43746.88, 61568.34) * mm});
            skLineSegment(sketch, "E724", {"start": v(44643.83, 60262.21) * mm, "end": v(44184.42, 60123.16) * mm});
            skLineSegment(sketch, "E725", {"start": v(44571.41, 60501.5) * mm, "end": v(43824.87, 60275.54) * mm});
            skLineSegment(sketch, "E726", {"start": v(46706.45, 60886.5) * mm, "end": v(45505.24, 60522.94) * mm});
            skLineSegment(sketch, "E727", {"start": v(46634.03, 61125.79) * mm, "end": v(45432.82, 60762.22) * mm});
            skLineSegment(sketch, "E728", {"start": v(48505.84, 61431.13) * mm, "end": v(47759.29, 61205.17) * mm});
            skLineSegment(sketch, "E729", {"start": v(48672.7, 61742.83) * mm, "end": v(47686.86, 61444.45) * mm});
            skLineSegment(sketch, "E730", {"start": v(45469.03, 60642.58) * mm, "end": v(45505.24, 60522.94) * mm});
            skLineSegment(sketch, "E731", {"start": v(44607.62, 60381.85) * mm, "end": v(44643.83, 60262.21) * mm});
            skLineSegment(sketch, "E732", {"start": v(45469.03, 60642.58) * mm, "end": v(45432.82, 60762.22) * mm});
            skLineSegment(sketch, "E733", {"start": v(44607.62, 60381.85) * mm, "end": v(44571.41, 60501.5) * mm});
            skLineSegment(sketch, "E734", {"start": v(44571.41, 60501.5) * mm, "end": v(45432.82, 60762.22) * mm});
            skLineSegment(sketch, "E735", {"start": v(44643.83, 60262.21) * mm, "end": v(45505.24, 60522.94) * mm});
            skLineSegment(sketch, "E736", {"start": v(47723.07, 61324.8) * mm, "end": v(47759.29, 61205.17) * mm});
            skLineSegment(sketch, "E737", {"start": v(46670.24, 61006.15) * mm, "end": v(46706.45, 60886.5) * mm});
            skLineSegment(sketch, "E738", {"start": v(47723.07, 61324.8) * mm, "end": v(47686.86, 61444.45) * mm});
            skLineSegment(sketch, "E739", {"start": v(46670.24, 61006.15) * mm, "end": v(46634.03, 61125.79) * mm});
            skLineSegment(sketch, "E740", {"start": v(46634.03, 61125.79) * mm, "end": v(47686.86, 61444.45) * mm});
            skLineSegment(sketch, "E741", {"start": v(46706.45, 60886.5) * mm, "end": v(47759.29, 61205.17) * mm});
            skLineSegment(sketch, "E742", {"start": v(48672.7, 61742.83) * mm, "end": v(49476.62, 59086.75) * mm});
            skLineSegment(sketch, "E743", {"start": v(48505.84, 61431.13) * mm, "end": v(49091.04, 59497.67) * mm});
            skLineSegment(sketch, "E744", {"start": v(44184.42, 60123.16) * mm, "end": v(44769.56, 58189.64) * mm});
            skLineSegment(sketch, "E745", {"start": v(43824.87, 60275.54) * mm, "end": v(44628.7, 57619.38) * mm});
            skLineSegment(sketch, "E746", {"start": v(46549.88, 58728.5) * mm, "end": v(45964.7, 60661.96) * mm});
            skLineSegment(sketch, "E747", {"start": v(46741.3, 58786.45) * mm, "end": v(46156.12, 60719.9) * mm});
            skLineSegment(sketch, "E748", {"start": v(49726, 58953.22) * mm, "end": v(44495.31, 57370.09) * mm});
            skLineSegment(sketch, "E749", {"start": v(49476.63, 59086.71) * mm, "end": v(44628.8, 57619.45) * mm});
            skLineSegment(sketch, "E750", {"start": v(49476.62, 59086.75) * mm, "end": v(44628.7, 57619.38) * mm});
            skLineSegment(sketch, "E751", {"start": v(49091.04, 59497.67) * mm, "end": v(46741.3, 58786.45) * mm});
            skLineSegment(sketch, "E752", {"start": v(44495.31, 57370.09) * mm, "end": v(44311.28, 57978.1) * mm});
            skLineSegment(sketch, "E753", {"start": v(44502.7, 58036.03) * mm, "end": v(44311.28, 57978.1) * mm});
            skLineSegment(sketch, "E754", {"start": v(44628.8, 57619.45) * mm, "end": v(44502.7, 58036.03) * mm});
            skLineSegment(sketch, "E755", {"start": v(60131.76, 53293.71) * mm, "end": v(60570.05, 52507.65) * mm});
            skLineSegment(sketch, "E756", {"start": v(60264.36, 52337.2) * mm, "end": v(60570.05, 52507.65) * mm});
            skLineSegment(sketch, "E757", {"start": v(59826.06, 53123.27) * mm, "end": v(60264.36, 52337.2) * mm});
            skLineSegment(sketch, "E758", {"start": v(59826.06, 53123.27) * mm, "end": v(60131.76, 53293.71) * mm});
            skLineSegment(sketch, "E759", {"start": v(47885.55, 61765.78) * mm, "end": v(48364.1, 61910.63) * mm});
            skLineSegment(sketch, "E760", {"start": v(47957.97, 61526.5) * mm, "end": v(48436.53, 61671.35) * mm});
            skLineSegment(sketch, "E761", {"start": v(47957.97, 61526.5) * mm, "end": v(47885.55, 61765.78) * mm});
            skLineSegment(sketch, "E762", {"start": v(34583.64, 74073.32) * mm, "end": v(34277.71, 74103.31) * mm});
            skLineSegment(sketch, "E763", {"start": v(36509.2, 74336.72) * mm, "end": v(36210.42, 74264.44) * mm});
            skLineSegment(sketch, "E764", {"start": v(38568.06, 74568.37) * mm, "end": v(38260.66, 74568.37) * mm});
            skLineSegment(sketch, "E765", {"start": v(40630.85, 74832.8) * mm, "end": v(40326.88, 74787.02) * mm});
            skLineSegment(sketch, "E766", {"start": v(42529.89, 75035.76) * mm, "end": v(42224.21, 75003.22) * mm});
            skLineSegment(sketch, "E767", {"start": v(44620.7, 75346.4) * mm, "end": v(44315.83, 75306.98) * mm});
            skLineSegment(sketch, "E768", {"start": v(46260.89, 75467.94) * mm, "end": v(45954.04, 75449.5) * mm});
            skLineSegment(sketch, "E769", {"start": v(48411.94, 75732.02) * mm, "end": v(48106.56, 75696.83) * mm});
            skLineSegment(sketch, "E770", {"start": v(34308.4, 74416.31) * mm, "end": v(34614.33, 74386.32) * mm});
            skLineSegment(sketch, "E771", {"start": v(34306.57, 74397.7) * mm, "end": v(34612.5, 74367.7) * mm});
            skLineSegment(sketch, "E772", {"start": v(34614.33, 74386.32) * mm, "end": v(34612.5, 74367.7) * mm});
            skLineSegment(sketch, "E773", {"start": v(34585.47, 74091.93) * mm, "end": v(34583.64, 74073.32) * mm});
            skLineSegment(sketch, "E774", {"start": v(34585.47, 74091.93) * mm, "end": v(34279.53, 74121.92) * mm});
            skLineSegment(sketch, "E775", {"start": v(34277.71, 74103.31) * mm, "end": v(34279.53, 74121.92) * mm});
            skLineSegment(sketch, "E776", {"start": v(34306.57, 74397.7) * mm, "end": v(34308.4, 74416.31) * mm});
            skLineSegment(sketch, "E777", {"start": v(34465.5, 74382.12) * mm, "end": v(34438.47, 74106.34) * mm});
            skLineSegment(sketch, "E778", {"start": v(34453.57, 74383.29) * mm, "end": v(34426.53, 74107.51) * mm});
            skLineSegment(sketch, "E779", {"start": v(36136.47, 74570.12) * mm, "end": v(36435.25, 74642.4) * mm});
            skLineSegment(sketch, "E780", {"start": v(36140.87, 74551.95) * mm, "end": v(36439.65, 74624.22) * mm});
            skLineSegment(sketch, "E781", {"start": v(36435.25, 74642.4) * mm, "end": v(36439.65, 74624.22) * mm});
            skLineSegment(sketch, "E782", {"start": v(36504.8, 74354.9) * mm, "end": v(36509.2, 74336.72) * mm});
            skLineSegment(sketch, "E783", {"start": v(36504.8, 74354.9) * mm, "end": v(36206.02, 74282.62) * mm});
            skLineSegment(sketch, "E784", {"start": v(36210.42, 74264.44) * mm, "end": v(36206.02, 74282.62) * mm});
            skLineSegment(sketch, "E785", {"start": v(36140.87, 74551.95) * mm, "end": v(36136.47, 74570.12) * mm});
            skLineSegment(sketch, "E786", {"start": v(36296.1, 74589.5) * mm, "end": v(36361.24, 74320.16) * mm});
            skLineSegment(sketch, "E787", {"start": v(36284.43, 74586.68) * mm, "end": v(36349.58, 74317.34) * mm});
            skLineSegment(sketch, "E788", {"start": v(38260.66, 74882.87) * mm, "end": v(38568.06, 74882.87) * mm});
            skLineSegment(sketch, "E789", {"start": v(38260.66, 74864.17) * mm, "end": v(38568.06, 74864.17) * mm});
            skLineSegment(sketch, "E790", {"start": v(38568.06, 74882.87) * mm, "end": v(38568.06, 74864.17) * mm});
            skLineSegment(sketch, "E791", {"start": v(38568.06, 74587.07) * mm, "end": v(38568.06, 74568.37) * mm});
            skLineSegment(sketch, "E792", {"start": v(38568.06, 74587.07) * mm, "end": v(38260.66, 74587.07) * mm});
            skLineSegment(sketch, "E793", {"start": v(38260.66, 74568.37) * mm, "end": v(38260.66, 74587.07) * mm});
            skLineSegment(sketch, "E794", {"start": v(38260.66, 74864.17) * mm, "end": v(38260.66, 74882.87) * mm});
            skLineSegment(sketch, "E795", {"start": v(38420.36, 74864.17) * mm, "end": v(38420.36, 74587.07) * mm});
            skLineSegment(sketch, "E796", {"start": v(38408.36, 74864.17) * mm, "end": v(38408.36, 74587.07) * mm});
            skLineSegment(sketch, "E797", {"start": v(40280.05, 75098.01) * mm, "end": v(40584.02, 75143.79) * mm});
            skLineSegment(sketch, "E798", {"start": v(40282.83, 75079.52) * mm, "end": v(40586.8, 75125.3) * mm});
            skLineSegment(sketch, "E799", {"start": v(40584.02, 75143.79) * mm, "end": v(40586.8, 75125.3) * mm});
            skLineSegment(sketch, "E800", {"start": v(40628.07, 74851.29) * mm, "end": v(40630.85, 74832.8) * mm});
            skLineSegment(sketch, "E801", {"start": v(40628.07, 74851.29) * mm, "end": v(40324.1, 74805.5) * mm});
            skLineSegment(sketch, "E802", {"start": v(40326.88, 74787.02) * mm, "end": v(40324.1, 74805.5) * mm});
            skLineSegment(sketch, "E803", {"start": v(40282.83, 75079.52) * mm, "end": v(40280.05, 75098.01) * mm});
            skLineSegment(sketch, "E804", {"start": v(40440.75, 75103.3) * mm, "end": v(40482.02, 74829.3) * mm});
            skLineSegment(sketch, "E805", {"start": v(40428.89, 75101.51) * mm, "end": v(40470.15, 74827.5) * mm});
            skLineSegment(sketch, "E806", {"start": v(42190.92, 75315.95) * mm, "end": v(42496.6, 75348.5) * mm});
            skLineSegment(sketch, "E807", {"start": v(42192.9, 75297.36) * mm, "end": v(42498.58, 75329.9) * mm});
            skLineSegment(sketch, "E808", {"start": v(42496.6, 75348.5) * mm, "end": v(42498.58, 75329.9) * mm});
            skLineSegment(sketch, "E809", {"start": v(42527.9, 75054.35) * mm, "end": v(42529.89, 75035.76) * mm});
            skLineSegment(sketch, "E810", {"start": v(42527.9, 75054.35) * mm, "end": v(42222.24, 75021.82) * mm});
            skLineSegment(sketch, "E811", {"start": v(42224.21, 75003.22) * mm, "end": v(42222.24, 75021.82) * mm});
            skLineSegment(sketch, "E812", {"start": v(42192.9, 75297.36) * mm, "end": v(42190.92, 75315.95) * mm});
            skLineSegment(sketch, "E813", {"start": v(42351.7, 75314.26) * mm, "end": v(42381.04, 75038.72) * mm});
            skLineSegment(sketch, "E814", {"start": v(42339.77, 75313) * mm, "end": v(42369.1, 75037.45) * mm});
            skLineSegment(sketch, "E815", {"start": v(44275.5, 75618.88) * mm, "end": v(44580.37, 75658.3) * mm});
            skLineSegment(sketch, "E816", {"start": v(44277.9, 75600.34) * mm, "end": v(44582.77, 75639.76) * mm});
            skLineSegment(sketch, "E817", {"start": v(44580.37, 75658.3) * mm, "end": v(44582.77, 75639.76) * mm});
            skLineSegment(sketch, "E818", {"start": v(44618.3, 75364.94) * mm, "end": v(44620.7, 75346.4) * mm});
            skLineSegment(sketch, "E819", {"start": v(44618.3, 75364.94) * mm, "end": v(44313.44, 75325.53) * mm});
            skLineSegment(sketch, "E820", {"start": v(44315.83, 75306.98) * mm, "end": v(44313.44, 75325.53) * mm});
            skLineSegment(sketch, "E821", {"start": v(44277.9, 75600.34) * mm, "end": v(44275.5, 75618.88) * mm});
            skLineSegment(sketch, "E822", {"start": v(44436.28, 75620.82) * mm, "end": v(44471.82, 75346) * mm});
            skLineSegment(sketch, "E823", {"start": v(44424.38, 75619.28) * mm, "end": v(44459.92, 75344.46) * mm});
            skLineSegment(sketch, "E824", {"start": v(45935.18, 75763.44) * mm, "end": v(46242.02, 75781.88) * mm});
            skLineSegment(sketch, "E825", {"start": v(45936.3, 75744.77) * mm, "end": v(46243.14, 75763.21) * mm});
            skLineSegment(sketch, "E826", {"start": v(46242.02, 75781.88) * mm, "end": v(46243.14, 75763.21) * mm});
            skLineSegment(sketch, "E827", {"start": v(46259.76, 75486.61) * mm, "end": v(46260.89, 75467.94) * mm});
            skLineSegment(sketch, "E828", {"start": v(46259.76, 75486.61) * mm, "end": v(45952.92, 75468.17) * mm});
            skLineSegment(sketch, "E829", {"start": v(45954.04, 75449.5) * mm, "end": v(45952.92, 75468.17) * mm});
            skLineSegment(sketch, "E830", {"start": v(45936.3, 75744.77) * mm, "end": v(45935.18, 75763.44) * mm});
            skLineSegment(sketch, "E831", {"start": v(46095.71, 75754.35) * mm, "end": v(46112.33, 75477.75) * mm});
            skLineSegment(sketch, "E832", {"start": v(46083.73, 75753.63) * mm, "end": v(46100.35, 75477.03) * mm});
            skLineSegment(sketch, "E833", {"start": v(48070.56, 76009.27) * mm, "end": v(48375.94, 76044.45) * mm});
            skLineSegment(sketch, "E834", {"start": v(48072.7, 75990.69) * mm, "end": v(48378.08, 76025.87) * mm});
            skLineSegment(sketch, "E835", {"start": v(48375.94, 76044.45) * mm, "end": v(48378.08, 76025.87) * mm});
            skLineSegment(sketch, "E836", {"start": v(48409.8, 75750.6) * mm, "end": v(48411.94, 75732.02) * mm});
            skLineSegment(sketch, "E837", {"start": v(48409.8, 75750.6) * mm, "end": v(48104.42, 75715.4) * mm});
            skLineSegment(sketch, "E838", {"start": v(48106.56, 75696.83) * mm, "end": v(48104.42, 75715.4) * mm});
            skLineSegment(sketch, "E839", {"start": v(48072.7, 75990.69) * mm, "end": v(48070.56, 76009.27) * mm});
            skLineSegment(sketch, "E840", {"start": v(48231.35, 76008.97) * mm, "end": v(48263.07, 75733.69) * mm});
            skLineSegment(sketch, "E841", {"start": v(48219.43, 76007.6) * mm, "end": v(48251.15, 75732.31) * mm});
            skLineSegment(sketch, "E842", {"start": v(34452, 74244.23) * mm, "end": v(34440.05, 74245.4) * mm});
            skLineSegment(sketch, "E843", {"start": v(36328.67, 74454.83) * mm, "end": v(36317, 74452) * mm});
            skLineSegment(sketch, "E844", {"start": v(38420.36, 74725.62) * mm, "end": v(38408.36, 74725.62) * mm});
            skLineSegment(sketch, "E845", {"start": v(40461.39, 74966.3) * mm, "end": v(40449.52, 74964.5) * mm});
            skLineSegment(sketch, "E846", {"start": v(42366.37, 75176.5) * mm, "end": v(42354.44, 75175.22) * mm});
            skLineSegment(sketch, "E847", {"start": v(44454.05, 75483.4) * mm, "end": v(44442.15, 75481.87) * mm});
            skLineSegment(sketch, "E848", {"start": v(46104.02, 75616.05) * mm, "end": v(46092.04, 75615.33) * mm});
            skLineSegment(sketch, "E849", {"start": v(48247.21, 75871.33) * mm, "end": v(48235.3, 75869.95) * mm});
            skCircle(sketch, "E850", {"center": v(34446.02, 74244.82) * mm, "radius": 300 * mm});
            skCircle(sketch, "E851", {"center": v(36322.84, 74453.42) * mm, "radius": 300 * mm});
            skCircle(sketch, "E852", {"center": v(38414.36, 74725.62) * mm, "radius": 300 * mm});
            skCircle(sketch, "E853", {"center": v(40455.45, 74965.4) * mm, "radius": 300 * mm});
            skCircle(sketch, "E854", {"center": v(42360.4, 75175.86) * mm, "radius": 300 * mm});
            skCircle(sketch, "E855", {"center": v(44448.1, 75482.64) * mm, "radius": 300 * mm});
            skCircle(sketch, "E856", {"center": v(46098.03, 75615.7) * mm, "radius": 300 * mm});
            skCircle(sketch, "E857", {"center": v(48241.25, 75870.64) * mm, "radius": 300 * mm});
            skCircle(sketch, "E858", {"center": v(34776.7, 58413.82) * mm, "radius": 328.69 * mm});
            skCircle(sketch, "E859", {"center": v(35224.5, 57091.4) * mm, "radius": 323.11 * mm});
            skCircle(sketch, "E860", {"center": v(35826.9, 55480) * mm, "radius": 308.82 * mm});
            skCircle(sketch, "E861", {"center": v(36309.94, 53902.1) * mm, "radius": 312.62 * mm});
            skCircle(sketch, "E862", {"center": v(36823.57, 52431.1) * mm, "radius": 314.17 * mm});
            skCircle(sketch, "E863", {"center": v(37258.05, 50987.66) * mm, "radius": 280.53 * mm});
            skLineSegment(sketch, "E864", {"start": v(44215.6, 60106.43) * mm, "end": v(45947.99, 60630.79) * mm});
            skLineSegment(sketch, "E865", {"start": v(45947.99, 60630.79) * mm, "end": v(46469.45, 58907.97) * mm});
            skLineSegment(sketch, "E866", {"start": v(46469.45, 58907.97) * mm, "end": v(44737.06, 58383.62) * mm});
            skLineSegment(sketch, "E867", {"start": v(44737.06, 58383.62) * mm, "end": v(44215.6, 60106.43) * mm});
            skLineSegment(sketch, "E868", {"start": v(44643.85, 60262.18) * mm, "end": v(45505.25, 60522.9) * mm});
            skLineSegment(sketch, "E869", {"start": v(49476.63, 59086.71) * mm, "end": v(49350.51, 59503.37) * mm});
            skLineSegment(sketch, "E870", {"start": v(49726, 58953.22) * mm, "end": v(49541.94, 59561.3) * mm});
            skLineSegment(sketch, "E871", {"start": v(51278.99, 57177.09) * mm, "end": v(56516.32, 58762.32) * mm});
            skLineSegment(sketch, "E872", {"start": v(56665.85, 58494.14) * mm, "end": v(51365.9, 56889.95) * mm});
            skLineSegment(sketch, "E873", {"start": v(50131.26, 70514.15) * mm, "end": v(50593.39, 70573.29) * mm});
            skLineSegment(sketch, "E874", {"start": v(50669.54, 69978.14) * mm, "end": v(50593.39, 70573.29) * mm});
            skLineSegment(sketch, "E875", {"start": v(49909.66, 69880.9) * mm, "end": v(50669.54, 69978.14) * mm});
            skLineSegment(sketch, "E876", {"start": v(47841.4, 61911.65) * mm, "end": v(48319.95, 62056.5) * mm});
            skLineSegment(sketch, "E877", {"start": v(48392.38, 61817.22) * mm, "end": v(48319.95, 62056.5) * mm});
            skLineSegment(sketch, "E878", {"start": v(47913.82, 61672.37) * mm, "end": v(48392.38, 61817.22) * mm});
            skLineSegment(sketch, "E879", {"start": v(47913.82, 61672.37) * mm, "end": v(47841.4, 61911.65) * mm});
            skLineSegment(sketch, "E880", {"start": v(58318.92, 63332.61) * mm, "end": v(58586.76, 62852.24) * mm});
            skLineSegment(sketch, "E881", {"start": v(58368.41, 62730.5) * mm, "end": v(58586.76, 62852.24) * mm});
            skLineSegment(sketch, "E882", {"start": v(58100.57, 63210.86) * mm, "end": v(58368.41, 62730.5) * mm});
            skLineSegment(sketch, "E883", {"start": v(58100.57, 63210.86) * mm, "end": v(58318.92, 63332.61) * mm});
            skLineSegment(sketch, "E884", {"start": v(59393.32, 61405.46) * mm, "end": v(59661.17, 60925.09) * mm});
            skLineSegment(sketch, "E885", {"start": v(59442.82, 60803.34) * mm, "end": v(59661.17, 60925.09) * mm});
            skLineSegment(sketch, "E886", {"start": v(59174.97, 61283.7) * mm, "end": v(59442.82, 60803.34) * mm});
            skLineSegment(sketch, "E887", {"start": v(59174.97, 61283.7) * mm, "end": v(59393.32, 61405.46) * mm});
            skLineSegment(sketch, "E888", {"start": v(61824.92, 57043.9) * mm, "end": v(62092.77, 56563.53) * mm});
            skLineSegment(sketch, "E889", {"start": v(61874.42, 56441.78) * mm, "end": v(62092.77, 56563.53) * mm});
            skLineSegment(sketch, "E890", {"start": v(61606.57, 56922.15) * mm, "end": v(61874.42, 56441.78) * mm});
            skLineSegment(sketch, "E891", {"start": v(61606.57, 56922.15) * mm, "end": v(61824.92, 57043.9) * mm});
            skLineSegment(sketch, "E892", {"start": v(62899.33, 55116.74) * mm, "end": v(63167.18, 54636.37) * mm});
            skLineSegment(sketch, "E893", {"start": v(62948.82, 54514.62) * mm, "end": v(63167.18, 54636.37) * mm});
            skLineSegment(sketch, "E894", {"start": v(62680.98, 54995) * mm, "end": v(62948.82, 54514.62) * mm});
            skLineSegment(sketch, "E895", {"start": v(62680.98, 54995) * mm, "end": v(62899.33, 55116.74) * mm});
            skLineSegment(sketch, "E896", {"start": v(55887.31, 67694.17) * mm, "end": v(56155.16, 67213.8) * mm});
            skLineSegment(sketch, "E897", {"start": v(55936.81, 67092.05) * mm, "end": v(56155.16, 67213.8) * mm});
            skLineSegment(sketch, "E898", {"start": v(55668.96, 67572.42) * mm, "end": v(55936.81, 67092.05) * mm});
            skLineSegment(sketch, "E899", {"start": v(55668.96, 67572.42) * mm, "end": v(55887.31, 67694.17) * mm});
            skLineSegment(sketch, "E900", {"start": v(54812.9, 69621.33) * mm, "end": v(55080.76, 69140.96) * mm});
            skLineSegment(sketch, "E901", {"start": v(54862.4, 69019.2) * mm, "end": v(55080.76, 69140.96) * mm});
            skLineSegment(sketch, "E902", {"start": v(54594.56, 69499.58) * mm, "end": v(54862.4, 69019.2) * mm});
            skLineSegment(sketch, "E903", {"start": v(54594.56, 69499.58) * mm, "end": v(54812.9, 69621.33) * mm});
            skLineSegment(sketch, "E904", {"start": v(56155.16, 67213.8) * mm, "end": v(55936.81, 67092.05) * mm});
            skLineSegment(sketch, "E905", {"start": v(55936.81, 67092.05) * mm, "end": v(55668.96, 67572.42) * mm});
            skLineSegment(sketch, "E906", {"start": v(57613.6, 55160.75) * mm, "end": v(58392.95, 55396.7) * mm});
            skLineSegment(sketch, "E907", {"start": v(59038.3, 52605.67) * mm, "end": v(59817.63, 52841.6) * mm});
            skLineSegment(sketch, "E908", {"start": v(52375.25, 73993.75) * mm, "end": v(52643.1, 73513.38) * mm});
            skLineSegment(sketch, "E909", {"start": v(52424.75, 73391.63) * mm, "end": v(52643.1, 73513.38) * mm});
            skLineSegment(sketch, "E910", {"start": v(52156.9, 73872) * mm, "end": v(52424.75, 73391.63) * mm});
            skLineSegment(sketch, "E911", {"start": v(52156.9, 73872) * mm, "end": v(52375.25, 73993.75) * mm});
            skLineSegment(sketch, "E912", {"start": v(52281.23, 65747.36) * mm, "end": v(53057.73, 65982.39) * mm});
            skLineSegment(sketch, "E913", {"start": v(52418.84, 65292.73) * mm, "end": v(53000.6, 65468.81) * mm});
            skLineSegment(sketch, "E914", {"start": v(52418.84, 65292.73) * mm, "end": v(52281.23, 65747.36) * mm});
            skLineSegment(sketch, "E915", {"start": v(54045.3, 63436.93) * mm, "end": v(55287.74, 59332.08) * mm});
            skLineSegment(sketch, "E916", {"start": v(53758.17, 63350.02) * mm, "end": v(54874.02, 59663.37) * mm});
            skLineSegment(sketch, "E917", {"start": v(53380.3, 65116.29) * mm, "end": v(53523.86, 65159.74) * mm});
            skLineSegment(sketch, "E918", {"start": v(53901.74, 63393.47) * mm, "end": v(54045.3, 63436.93) * mm});
            skLineSegment(sketch, "E919", {"start": v(53380.3, 65116.29) * mm, "end": v(53236.72, 65072.83) * mm});
            skLineSegment(sketch, "E920", {"start": v(53901.74, 63393.47) * mm, "end": v(53758.17, 63350.02) * mm});
            skLineSegment(sketch, "E921", {"start": v(53758.17, 63350.02) * mm, "end": v(53236.72, 65072.83) * mm});
            skLineSegment(sketch, "E922", {"start": v(54045.3, 63436.93) * mm, "end": v(53523.86, 65159.74) * mm});
            skLineSegment(sketch, "E923", {"start": v(53236.72, 65072.83) * mm, "end": v(53758.17, 63350.02) * mm});
            skLineSegment(sketch, "E924", {"start": v(53523.86, 65159.74) * mm, "end": v(54045.3, 63436.93) * mm});
            skLineSegment(sketch, "E925", {"start": v(35194.47, 68817.29) * mm, "end": v(34817.9, 70061.55) * mm});
            skLineSegment(sketch, "E926", {"start": v(35105.03, 70148.46) * mm, "end": v(34817.9, 70061.55) * mm});
            skLineSegment(sketch, "E927", {"start": v(35481.6, 68904.2) * mm, "end": v(35105.03, 70148.46) * mm});
            skLineSegment(sketch, "E928", {"start": v(35481.6, 68904.2) * mm, "end": v(35194.47, 68817.29) * mm});
            skLineSegment(sketch, "E929", {"start": v(42377.52, 61153.87) * mm, "end": v(42261.62, 61536.8) * mm});
            skLineSegment(sketch, "E930", {"start": v(42740.18, 61681.65) * mm, "end": v(42261.62, 61536.8) * mm});
            skLineSegment(sketch, "E931", {"start": v(42856.08, 61298.72) * mm, "end": v(42740.18, 61681.65) * mm});
            skLineSegment(sketch, "E932", {"start": v(53225.02, 65066.3) * mm, "end": v(53000.6, 65468.81) * mm});
            skLineSegment(sketch, "E933", {"start": v(53487.04, 65212.4) * mm, "end": v(53057.73, 65982.39) * mm});
            skLineSegment(sketch, "E934", {"start": v(59287.5, 52158.7) * mm, "end": v(53342.63, 50359.31) * mm});
            skLineSegment(sketch, "E935", {"start": v(58991.9, 52278.2) * mm, "end": v(53284.69, 50550.73) * mm});
            skLineSegment(sketch, "E936", {"start": v(58991.9, 52278.2) * mm, "end": v(59187.82, 52337.5) * mm});
            skLineSegment(sketch, "E937", {"start": v(55287.74, 59332.08) * mm, "end": v(59187.82, 52337.5) * mm});
            skLineSegment(sketch, "E938", {"start": v(54874.02, 59663.37) * mm, "end": v(58991.9, 52278.2) * mm});
            skLineSegment(sketch, "E939", {"start": v(61463.3, 49888.88) * mm, "end": v(61702.18, 49961.19) * mm});
            skLineSegment(sketch, "E940", {"start": v(61702.18, 49961.19) * mm, "end": v(61774.6, 49721.9) * mm});
            skLineSegment(sketch, "E941", {"start": v(61774.6, 49721.9) * mm, "end": v(61535.73, 49649.6) * mm});
            skLineSegment(sketch, "E942", {"start": v(61535.73, 49649.6) * mm, "end": v(61463.3, 49888.88) * mm});
            skLineSegment(sketch, "E943", {"start": v(53291.1, 65935.67) * mm, "end": v(53529.97, 66007.97) * mm});
            skLineSegment(sketch, "E944", {"start": v(53529.97, 66007.97) * mm, "end": v(53602.4, 65768.7) * mm});
            skLineSegment(sketch, "E945", {"start": v(53602.4, 65768.7) * mm, "end": v(53363.52, 65696.4) * mm});
            skLineSegment(sketch, "E946", {"start": v(53363.52, 65696.4) * mm, "end": v(53291.1, 65935.67) * mm});
            skLineSegment(sketch, "E947", {"start": v(65900.3, 51172.38) * mm, "end": v(66118.29, 51293.9) * mm});
            skLineSegment(sketch, "E948", {"start": v(66118.29, 51293.9) * mm, "end": v(66240.02, 51075.55) * mm});
            skLineSegment(sketch, "E949", {"start": v(66240.02, 51075.55) * mm, "end": v(66022.03, 50954.02) * mm});
            skLineSegment(sketch, "E950", {"start": v(66022.03, 50954.02) * mm, "end": v(65900.3, 51172.38) * mm});
            skLineSegment(sketch, "E951", {"start": v(43166.65, 61878.55) * mm, "end": v(43405.52, 61950.85) * mm});
            skLineSegment(sketch, "E952", {"start": v(43405.52, 61950.85) * mm, "end": v(43477.94, 61711.57) * mm});
            skLineSegment(sketch, "E953", {"start": v(43477.94, 61711.57) * mm, "end": v(43239.07, 61639.27) * mm});
            skLineSegment(sketch, "E954", {"start": v(43239.07, 61639.27) * mm, "end": v(43166.65, 61878.55) * mm});
            skLineSegment(sketch, "E955", {"start": v(48366.02, 61911.21) * mm, "end": v(48604.9, 61983.51) * mm});
            skLineSegment(sketch, "E956", {"start": v(48604.9, 61983.51) * mm, "end": v(48677.32, 61744.23) * mm});
            skLineSegment(sketch, "E957", {"start": v(48677.32, 61744.23) * mm, "end": v(48438.45, 61671.93) * mm});
            skLineSegment(sketch, "E958", {"start": v(48438.45, 61671.93) * mm, "end": v(48366.02, 61911.21) * mm});
            skLineSegment(sketch, "E959", {"start": v(64065.34, 54464.23) * mm, "end": v(64283.47, 54585.5) * mm});
            skLineSegment(sketch, "E960", {"start": v(64283.47, 54585.5) * mm, "end": v(64404.95, 54367) * mm});
            skLineSegment(sketch, "E961", {"start": v(64404.95, 54367) * mm, "end": v(64186.82, 54245.73) * mm});
            skLineSegment(sketch, "E962", {"start": v(64186.82, 54245.73) * mm, "end": v(64065.34, 54464.23) * mm});
            skLineSegment(sketch, "E963", {"start": v(45953.73, 61181.06) * mm, "end": v(46192.6, 61253.36) * mm});
            skLineSegment(sketch, "E964", {"start": v(46192.6, 61253.36) * mm, "end": v(46265.03, 61014.08) * mm});
            skLineSegment(sketch, "E965", {"start": v(46265.03, 61014.08) * mm, "end": v(46026.16, 60941.78) * mm});
            skLineSegment(sketch, "E966", {"start": v(46026.16, 60941.78) * mm, "end": v(45953.73, 61181.06) * mm});
            skLineSegment(sketch, "E967", {"start": v(52418.02, 67337.58) * mm, "end": v(52656.9, 67409.89) * mm});
            skLineSegment(sketch, "E968", {"start": v(52656.9, 67409.89) * mm, "end": v(52729.32, 67170.6) * mm});
            skLineSegment(sketch, "E969", {"start": v(52729.32, 67170.6) * mm, "end": v(52490.45, 67098.3) * mm});
            skLineSegment(sketch, "E970", {"start": v(52490.45, 67098.3) * mm, "end": v(52418.02, 67337.58) * mm});
            skLineSegment(sketch, "E971", {"start": v(4.94, 5000) * mm, "end": v(0, -5000) * mm});
            skLineSegment(sketch, "E972", {"start": v(5000, 0) * mm, "end": v(-5000, -4.94) * mm});
            skCircle(sketch, "E973", {"center": v(0, -2.47) * mm, "radius": 1929.43 * mm});
            skLineSegment(sketch, "E974", {"start": v(58325.52, 53471.87) * mm, "end": v(58500.2, 53569.27) * mm});
            skLineSegment(sketch, "E975", {"start": v(58500.2, 53569.27) * mm, "end": v(58889.8, 52870.55) * mm});
            skLineSegment(sketch, "E976", {"start": v(58889.8, 52870.55) * mm, "end": v(58715.12, 52773.15) * mm});
            skLineSegment(sketch, "E977", {"start": v(58715.12, 52773.15) * mm, "end": v(58325.52, 53471.87) * mm});
            skLineSegment(sketch, "E978", {"start": v(32883.91, 66080.85) * mm, "end": v(33122.79, 66153.15) * mm});
            skLineSegment(sketch, "E979", {"start": v(33122.79, 66153.15) * mm, "end": v(33195.21, 65913.87) * mm});
            skLineSegment(sketch, "E980", {"start": v(33195.21, 65913.87) * mm, "end": v(32956.34, 65841.57) * mm});
            skLineSegment(sketch, "E981", {"start": v(32956.34, 65841.57) * mm, "end": v(32883.91, 66080.85) * mm});
            skLineSegment(sketch, "E982", {"start": v(32882.84, 66524.7) * mm, "end": v(32930.7, 66539.19) * mm});
            skLineSegment(sketch, "E983", {"start": v(44381.57, 66109.13) * mm, "end": v(46379.94, 66189.81) * mm});
            skLineSegment(sketch, "E984", {"start": v(46379.94, 66189.81) * mm, "end": v(46460.62, 64191.44) * mm});
            skLineSegment(sketch, "E985", {"start": v(46460.62, 64191.44) * mm, "end": v(44462.25, 64110.76) * mm});
            skLineSegment(sketch, "E986", {"start": v(44462.25, 64110.76) * mm, "end": v(44381.57, 66109.13) * mm});
            skLineSegment(sketch, "E987", {"start": v(44462.25, 64110.76) * mm, "end": v(46379.94, 66189.81) * mm});
            skLineSegment(sketch, "E988", {"start": v(44381.57, 66109.13) * mm, "end": v(46460.62, 64191.44) * mm});
            skCircle(sketch, "E989", {"center": v(42435, 71860) * mm, "radius": 350 * mm});
            skLineSegment(sketch, "E990", {"start": v(51034.44, 72929.32) * mm, "end": v(49850.78, 74290.55) * mm});
            skLineSegment(sketch, "E991", {"start": v(53640.78, 69956.14) * mm, "end": v(52836.54, 68341.45) * mm});
            skLineSegment(sketch, "E992", {"start": v(53830.5, 68468.18) * mm, "end": v(52646.83, 69829.4) * mm});
            skLineSegment(sketch, "E993", {"start": v(37274.9, 65820.2) * mm, "end": v(38473.93, 65868.61) * mm});
            skLineSegment(sketch, "E994", {"start": v(38473.93, 65868.61) * mm, "end": v(38510.16, 64971.35) * mm});
            skLineSegment(sketch, "E995", {"start": v(38510.16, 64971.35) * mm, "end": v(37311.13, 64922.95) * mm});
            skLineSegment(sketch, "E996", {"start": v(37311.13, 64922.95) * mm, "end": v(37274.9, 65820.2) * mm});
            skLineSegment(sketch, "E997", {"start": v(50791.39, 66363.5) * mm, "end": v(51990.41, 66411.9) * mm});
            skLineSegment(sketch, "E998", {"start": v(51990.41, 66411.9) * mm, "end": v(52026.64, 65514.65) * mm});
            skLineSegment(sketch, "E999", {"start": v(52026.64, 65514.65) * mm, "end": v(50827.61, 65466.24) * mm});
            skLineSegment(sketch, "E1000", {"start": v(50827.61, 65466.24) * mm, "end": v(50791.39, 66363.5) * mm});
            skLineSegment(sketch, "E1001", {"start": v(50791.39, 66363.5) * mm, "end": v(52026.64, 65514.65) * mm});
            skLineSegment(sketch, "E1002", {"start": v(51990.41, 66411.9) * mm, "end": v(50827.61, 65466.24) * mm});
            skLineSegment(sketch, "E1003", {"start": v(37311.13, 64922.95) * mm, "end": v(38473.93, 65868.61) * mm});
            skLineSegment(sketch, "E1004", {"start": v(38510.16, 64971.35) * mm, "end": v(37274.9, 65820.2) * mm});
            skLineSegment(sketch, "E1005", {"start": v(54534.84, 63584.32) * mm, "end": v(54187.28, 64732.89) * mm});
            skLineSegment(sketch, "E1006", {"start": v(54187.28, 64732.89) * mm, "end": v(55046.78, 64992.97) * mm});
            skLineSegment(sketch, "E1007", {"start": v(55046.78, 64992.97) * mm, "end": v(55394.34, 63844.4) * mm});
            skLineSegment(sketch, "E1008", {"start": v(55394.34, 63844.4) * mm, "end": v(54534.84, 63584.32) * mm});
            skLineSegment(sketch, "E1009", {"start": v(54534.84, 63584.32) * mm, "end": v(55046.78, 64992.97) * mm});
            skLineSegment(sketch, "E1010", {"start": v(54187.28, 64732.89) * mm, "end": v(55394.34, 63844.4) * mm});
            skLineSegment(sketch, "E1011", {"start": v(59168.74, 53933.32) * mm, "end": v(58821.16, 55081.88) * mm});
            skLineSegment(sketch, "E1012", {"start": v(58821.16, 55081.88) * mm, "end": v(59680.65, 55341.98) * mm});
            skLineSegment(sketch, "E1013", {"start": v(59680.65, 55341.98) * mm, "end": v(60028.23, 54193.42) * mm});
            skLineSegment(sketch, "E1014", {"start": v(60028.23, 54193.42) * mm, "end": v(59168.74, 53933.32) * mm});
            skLineSegment(sketch, "E1015", {"start": v(59168.74, 53933.32) * mm, "end": v(59680.65, 55341.98) * mm});
            skLineSegment(sketch, "E1016", {"start": v(58821.16, 55081.88) * mm, "end": v(60028.23, 54193.42) * mm});
            skLineSegment(sketch, "E1017", {"start": v(44184.43, 60123.13) * mm, "end": v(44567.28, 60238.99) * mm});
            skLineSegment(sketch, "E1018", {"start": v(44567.28, 60238.99) * mm, "end": v(44683.15, 59856.14) * mm});
            skLineSegment(sketch, "E1019", {"start": v(44683.15, 59856.14) * mm, "end": v(44300.3, 59740.27) * mm});
            skLineSegment(sketch, "E1020", {"start": v(44300.3, 59740.27) * mm, "end": v(44184.43, 60123.13) * mm});
            skLineSegment(sketch, "E1021", {"start": v(44567.28, 60238.99) * mm, "end": v(44300.3, 59740.27) * mm});
            skLineSegment(sketch, "E1022", {"start": v(44683.15, 59856.14) * mm, "end": v(44184.43, 60123.13) * mm});
            skLineSegment(sketch, "E1023", {"start": v(34476.97, 72521.3) * mm, "end": v(35369.84, 72634.42) * mm});
            skLineSegment(sketch, "E1024", {"start": v(35369.84, 72634.42) * mm, "end": v(35659.25, 70350.2) * mm});
            skLineSegment(sketch, "E1025", {"start": v(35659.25, 70350.2) * mm, "end": v(34766.39, 70237.07) * mm});
            skLineSegment(sketch, "E1026", {"start": v(34766.39, 70237.07) * mm, "end": v(34476.97, 72521.3) * mm});
            skLineSegment(sketch, "E1027", {"start": v(49850.78, 74290.55) * mm, "end": v(50844.73, 74417.28) * mm});
            skLineSegment(sketch, "E1028", {"start": v(50844.73, 74417.28) * mm, "end": v(51034.44, 72929.32) * mm});
            skLineSegment(sketch, "E1029", {"start": v(51034.44, 72929.32) * mm, "end": v(50040.49, 72802.6) * mm});
            skLineSegment(sketch, "E1030", {"start": v(50040.49, 72802.6) * mm, "end": v(49850.78, 74290.55) * mm});
            skLineSegment(sketch, "E1031", {"start": v(52423.14, 70002.5) * mm, "end": v(53813.88, 70179.82) * mm});
            skLineSegment(sketch, "E1032", {"start": v(53813.88, 70179.82) * mm, "end": v(54054.18, 68295.08) * mm});
            skLineSegment(sketch, "E1033", {"start": v(54054.18, 68295.08) * mm, "end": v(52663.44, 68117.76) * mm});
            skLineSegment(sketch, "E1034", {"start": v(52663.44, 68117.76) * mm, "end": v(52423.14, 70002.5) * mm});
            skLineSegment(sketch, "E1035", {"start": v(52646.83, 69829.4) * mm, "end": v(53640.78, 69956.14) * mm});
            skLineSegment(sketch, "E1036", {"start": v(53640.78, 69956.14) * mm, "end": v(53830.5, 68468.18) * mm});
            skLineSegment(sketch, "E1037", {"start": v(53830.5, 68468.18) * mm, "end": v(52836.54, 68341.45) * mm});
            skLineSegment(sketch, "E1038", {"start": v(52836.54, 68341.45) * mm, "end": v(52646.83, 69829.4) * mm});
            skLineSegment(sketch, "E1039", {"start": v(34700.56, 72348.02) * mm, "end": v(35196.66, 72410.88) * mm});
            skLineSegment(sketch, "E1040", {"start": v(35196.66, 72410.88) * mm, "end": v(35297.47, 71615.2) * mm});
            skLineSegment(sketch, "E1041", {"start": v(35297.47, 71615.2) * mm, "end": v(34801.37, 71552.35) * mm});
            skLineSegment(sketch, "E1042", {"start": v(34801.37, 71552.35) * mm, "end": v(34700.56, 72348.02) * mm});
            skLineSegment(sketch, "E1043", {"start": v(34839.58, 71254.46) * mm, "end": v(35336.24, 71317.88) * mm});
            skLineSegment(sketch, "E1044", {"start": v(35336.24, 71317.88) * mm, "end": v(35437.55, 70524.61) * mm});
            skLineSegment(sketch, "E1045", {"start": v(35437.55, 70524.61) * mm, "end": v(34940.89, 70461.18) * mm});
            skLineSegment(sketch, "E1046", {"start": v(34940.89, 70461.18) * mm, "end": v(34839.58, 71254.46) * mm});
            skLineSegment(sketch, "E1047", {"start": v(50844.73, 74417.28) * mm, "end": v(50040.49, 72802.6) * mm});
            skLineSegment(sketch, "E1048", {"start": v(34801.37, 71552.35) * mm, "end": v(35196.66, 72410.88) * mm});
            skLineSegment(sketch, "E1049", {"start": v(35297.47, 71615.2) * mm, "end": v(34700.56, 72348.02) * mm});
            skLineSegment(sketch, "E1050", {"start": v(34839.58, 71254.46) * mm, "end": v(35437.55, 70524.61) * mm});
            skLineSegment(sketch, "E1051", {"start": v(35336.24, 71317.88) * mm, "end": v(34940.89, 70461.18) * mm});
            skLineSegment(sketch, "E1052", {"start": v(49627.09, 74463.65) * mm, "end": v(51017.83, 74640.97) * mm});
            skLineSegment(sketch, "E1053", {"start": v(51017.83, 74640.97) * mm, "end": v(51258.13, 72756.22) * mm});
            skLineSegment(sketch, "E1054", {"start": v(51258.13, 72756.22) * mm, "end": v(49867.4, 72578.9) * mm});
            skLineSegment(sketch, "E1055", {"start": v(49867.4, 72578.9) * mm, "end": v(49627.09, 74463.65) * mm});
            skLineSegment(sketch, "E1056", {"start": v(38189.93, 60372.24) * mm, "end": v(38428.8, 60444.54) * mm});
            skLineSegment(sketch, "E1057", {"start": v(38428.8, 60444.54) * mm, "end": v(38501.23, 60205.27) * mm});
            skLineSegment(sketch, "E1058", {"start": v(38501.23, 60205.27) * mm, "end": v(38262.36, 60132.96) * mm});
            skLineSegment(sketch, "E1059", {"start": v(38262.36, 60132.96) * mm, "end": v(38189.93, 60372.24) * mm});
            skLineSegment(sketch, "E1060", {"start": v(59738.14, 53370.87) * mm, "end": v(59956.13, 53492.41) * mm});
            skLineSegment(sketch, "E1061", {"start": v(59956.13, 53492.41) * mm, "end": v(60077.88, 53274.06) * mm});
            skLineSegment(sketch, "E1062", {"start": v(60077.88, 53274.06) * mm, "end": v(59859.9, 53152.52) * mm});
            skLineSegment(sketch, "E1063", {"start": v(59859.9, 53152.52) * mm, "end": v(59738.14, 53370.87) * mm});
            skLineSegment(sketch, "E1064", {"start": v(55210.51, 59594.72) * mm, "end": v(55449.39, 59667.03) * mm});
            skLineSegment(sketch, "E1065", {"start": v(55449.39, 59667.03) * mm, "end": v(55521.81, 59427.75) * mm});
            skLineSegment(sketch, "E1066", {"start": v(55521.81, 59427.75) * mm, "end": v(55282.94, 59355.44) * mm});
            skLineSegment(sketch, "E1067", {"start": v(55282.94, 59355.44) * mm, "end": v(55210.51, 59594.72) * mm});
            skLineSegment(sketch, "E1068", {"start": v(55647.75, 58840.53) * mm, "end": v(55886.63, 58912.83) * mm});
            skLineSegment(sketch, "E1069", {"start": v(55886.63, 58912.83) * mm, "end": v(55959.05, 58673.55) * mm});
            skLineSegment(sketch, "E1070", {"start": v(55959.05, 58673.55) * mm, "end": v(55720.18, 58601.25) * mm});
            skLineSegment(sketch, "E1071", {"start": v(55720.18, 58601.25) * mm, "end": v(55647.75, 58840.53) * mm});
            skLineSegment(sketch, "E1072", {"start": v(37456.34, 66947.4) * mm, "end": v(37703.9, 66979.13) * mm});
            skLineSegment(sketch, "E1073", {"start": v(37703.9, 66979.13) * mm, "end": v(37735.69, 66731.16) * mm});
            skLineSegment(sketch, "E1074", {"start": v(37735.69, 66731.16) * mm, "end": v(37488.14, 66699.42) * mm});
            skLineSegment(sketch, "E1075", {"start": v(37488.14, 66699.42) * mm, "end": v(37456.34, 66947.4) * mm});
            skLineSegment(sketch, "E1076", {"start": v(47002.58, 67097.48) * mm, "end": v(47250.1, 67129.43) * mm});
            skLineSegment(sketch, "E1077", {"start": v(47250.1, 67129.43) * mm, "end": v(47282.11, 66881.48) * mm});
            skLineSegment(sketch, "E1078", {"start": v(47282.11, 66881.48) * mm, "end": v(47034.59, 66849.54) * mm});
            skLineSegment(sketch, "E1079", {"start": v(47034.59, 66849.54) * mm, "end": v(47002.58, 67097.48) * mm});
            skCircle(sketch, "E1080", {"center": v(59907.57, 53323.26) * mm, "radius": 100 * mm});
            skLineSegment(sketch, "E1081", {"start": v(54853.3, 52162.53) * mm, "end": v(55092.18, 52234.83) * mm});
            skLineSegment(sketch, "E1082", {"start": v(55092.18, 52234.83) * mm, "end": v(55164.6, 51995.55) * mm});
            skLineSegment(sketch, "E1083", {"start": v(55164.6, 51995.55) * mm, "end": v(54925.73, 51923.25) * mm});
            skLineSegment(sketch, "E1084", {"start": v(54925.73, 51923.25) * mm, "end": v(54853.3, 52162.53) * mm});
            skCircle(sketch, "E1085", {"center": v(61618.95, 49805.4) * mm, "radius": 100 * mm});
            skCircle(sketch, "E1086", {"center": v(66070.16, 51123.96) * mm, "radius": 100 * mm});
            skCircle(sketch, "E1087", {"center": v(64235.09, 54415.48) * mm, "radius": 100 * mm});
            skCircle(sketch, "E1088", {"center": v(55008.95, 52079.04) * mm, "radius": 100 * mm});
            skCircle(sketch, "E1089", {"center": v(55803.4, 58757.04) * mm, "radius": 100 * mm});
            skCircle(sketch, "E1090", {"center": v(55366.16, 59511.24) * mm, "radius": 100 * mm});
            skLineSegment(sketch, "E1091", {"start": v(54484.83, 61992.3) * mm, "end": v(54723.7, 62064.61) * mm});
            skLineSegment(sketch, "E1092", {"start": v(54723.7, 62064.61) * mm, "end": v(54796.13, 61825.33) * mm});
            skLineSegment(sketch, "E1093", {"start": v(54796.13, 61825.33) * mm, "end": v(54557.25, 61753.03) * mm});
            skLineSegment(sketch, "E1094", {"start": v(54557.25, 61753.03) * mm, "end": v(54484.83, 61992.3) * mm});
            skCircle(sketch, "E1095", {"center": v(54640.48, 61908.82) * mm, "radius": 100 * mm});
            skLineSegment(sketch, "E1096", {"start": v(54197.3, 62934.76) * mm, "end": v(54436.17, 63007.06) * mm});
            skLineSegment(sketch, "E1097", {"start": v(54436.17, 63007.06) * mm, "end": v(54508.6, 62767.78) * mm});
            skLineSegment(sketch, "E1098", {"start": v(54508.6, 62767.78) * mm, "end": v(54269.72, 62695.48) * mm});
            skLineSegment(sketch, "E1099", {"start": v(54269.72, 62695.48) * mm, "end": v(54197.3, 62934.76) * mm});
            skCircle(sketch, "E1100", {"center": v(54352.95, 62851.27) * mm, "radius": 100 * mm});
            skCircle(sketch, "E1101", {"center": v(53446.75, 65852.18) * mm, "radius": 100 * mm});
            skCircle(sketch, "E1102", {"center": v(52573.67, 67254.1) * mm, "radius": 100 * mm});
            skCircle(sketch, "E1103", {"center": v(47142.35, 66989.48) * mm, "radius": 100 * mm});
            skCircle(sketch, "E1104", {"center": v(37596.02, 66839.28) * mm, "radius": 100 * mm});
            skCircle(sketch, "E1105", {"center": v(33039.56, 65997.36) * mm, "radius": 100 * mm});
            skCircle(sketch, "E1106", {"center": v(34791.84, 60208.14) * mm, "radius": 100 * mm});
            skCircle(sketch, "E1107", {"center": v(36052.03, 56044.68) * mm, "radius": 100 * mm});
            skCircle(sketch, "E1108", {"center": v(38345.58, 60288.75) * mm, "radius": 100 * mm});
            skCircle(sketch, "E1109", {"center": v(43322.3, 61795.06) * mm, "radius": 100 * mm});
            skCircle(sketch, "E1110", {"center": v(46109.38, 61097.57) * mm, "radius": 100 * mm});
            skCircle(sketch, "E1111", {"center": v(48521.67, 61827.72) * mm, "radius": 100 * mm});
            skLineSegment(sketch, "E1112", {"start": v(50038.27, 60390.66) * mm, "end": v(50277.14, 60462.96) * mm});
            skLineSegment(sketch, "E1113", {"start": v(50277.14, 60462.96) * mm, "end": v(50349.57, 60223.68) * mm});
            skLineSegment(sketch, "E1114", {"start": v(50349.57, 60223.68) * mm, "end": v(50110.7, 60151.38) * mm});
            skLineSegment(sketch, "E1115", {"start": v(50110.7, 60151.38) * mm, "end": v(50038.27, 60390.66) * mm});
            skCircle(sketch, "E1116", {"center": v(50193.92, 60307.17) * mm, "radius": 100 * mm});
            skLineSegment(sketch, "E1117", {"start": v(60178.25, 61433.16) * mm, "end": v(60396.38, 61554.44) * mm});
            skLineSegment(sketch, "E1118", {"start": v(60396.38, 61554.44) * mm, "end": v(60517.86, 61335.93) * mm});
            skLineSegment(sketch, "E1119", {"start": v(60517.86, 61335.93) * mm, "end": v(60299.73, 61214.66) * mm});
            skLineSegment(sketch, "E1120", {"start": v(60299.73, 61214.66) * mm, "end": v(60178.25, 61433.16) * mm});
            skCircle(sketch, "E1121", {"center": v(60348, 61384.4) * mm, "radius": 100 * mm});
            skLineSegment(sketch, "E1122", {"start": v(57546.85, 54869.81) * mm, "end": v(57721.53, 54967.21) * mm});
            skLineSegment(sketch, "E1123", {"start": v(57721.53, 54967.21) * mm, "end": v(58208.52, 54093.8) * mm});
            skLineSegment(sketch, "E1124", {"start": v(58208.52, 54093.8) * mm, "end": v(58033.84, 53996.4) * mm});
            skLineSegment(sketch, "E1125", {"start": v(58033.84, 53996.4) * mm, "end": v(57546.85, 54869.81) * mm});
            skLineSegment(sketch, "E1126", {"start": v(56914.07, 56005.42) * mm, "end": v(57088.75, 56102.82) * mm});
            skLineSegment(sketch, "E1127", {"start": v(57088.75, 56102.82) * mm, "end": v(57283.55, 55753.45) * mm});
            skLineSegment(sketch, "E1128", {"start": v(57283.55, 55753.45) * mm, "end": v(57108.87, 55656.05) * mm});
            skLineSegment(sketch, "E1129", {"start": v(57108.87, 55656.05) * mm, "end": v(56914.07, 56005.42) * mm});
            skLineSegment(sketch, "E1130", {"start": v(49409.97, 64434.35) * mm, "end": v(49301.3, 64793.37) * mm});
            skLineSegment(sketch, "E1131", {"start": v(49301.3, 64793.37) * mm, "end": v(50067, 65025.12) * mm});
            skLineSegment(sketch, "E1132", {"start": v(50067, 65025.12) * mm, "end": v(50175.66, 64666.1) * mm});
            skLineSegment(sketch, "E1133", {"start": v(50175.66, 64666.1) * mm, "end": v(49409.97, 64434.35) * mm});
            skLineSegment(sketch, "E1134", {"start": v(34636.19, 60291.63) * mm, "end": v(34875.06, 60363.93) * mm});
            skLineSegment(sketch, "E1135", {"start": v(34875.06, 60363.93) * mm, "end": v(34947.49, 60124.65) * mm});
            skLineSegment(sketch, "E1136", {"start": v(34947.49, 60124.65) * mm, "end": v(34708.61, 60052.35) * mm});
            skLineSegment(sketch, "E1137", {"start": v(34708.61, 60052.35) * mm, "end": v(34636.19, 60291.63) * mm});
            skLineSegment(sketch, "E1138", {"start": v(35896.38, 56128.17) * mm, "end": v(36135.26, 56200.47) * mm});
            skLineSegment(sketch, "E1139", {"start": v(36135.26, 56200.47) * mm, "end": v(36207.68, 55961.2) * mm});
            skLineSegment(sketch, "E1140", {"start": v(36207.68, 55961.2) * mm, "end": v(35968.8, 55888.9) * mm});
            skLineSegment(sketch, "E1141", {"start": v(35968.8, 55888.9) * mm, "end": v(35896.38, 56128.17) * mm});
            skLineSegment(sketch, "E1142", {"start": v(36403, 64574.74) * mm, "end": v(36761.93, 64683.38) * mm});
            skLineSegment(sketch, "E1143", {"start": v(36761.93, 64683.38) * mm, "end": v(36993.68, 63917.69) * mm});
            skLineSegment(sketch, "E1144", {"start": v(36993.68, 63917.69) * mm, "end": v(36634.75, 63809.05) * mm});
            skLineSegment(sketch, "E1145", {"start": v(36634.75, 63809.05) * mm, "end": v(36403, 64574.74) * mm});
            skLineSegment(sketch, "E1146", {"start": v(33524.84, 66731.22) * mm, "end": v(33811.96, 66818.19) * mm});
            skLineSegment(sketch, "E1147", {"start": v(33811.96, 66818.19) * mm, "end": v(33920.67, 66459.29) * mm});
            skLineSegment(sketch, "E1148", {"start": v(33920.67, 66459.29) * mm, "end": v(33633.56, 66372.32) * mm});
            skLineSegment(sketch, "E1149", {"start": v(33633.56, 66372.32) * mm, "end": v(33524.84, 66731.22) * mm});
            skLineSegment(sketch, "E1150", {"start": v(40221.97, 65782.56) * mm, "end": v(40523.97, 65560.26) * mm});
            skLineSegment(sketch, "E1151", {"start": v(40523.97, 65560.26) * mm, "end": v(39931.17, 64754.91) * mm});
            skLineSegment(sketch, "E1152", {"start": v(39931.17, 64754.91) * mm, "end": v(39629.16, 64977.22) * mm});
            skLineSegment(sketch, "E1153", {"start": v(39629.16, 64977.22) * mm, "end": v(40221.97, 65782.56) * mm});
            skLineSegment(sketch, "E1154", {"start": v(47169.33, 67854.25) * mm, "end": v(47541.16, 67902.9) * mm});
            skLineSegment(sketch, "E1155", {"start": v(47541.16, 67902.9) * mm, "end": v(47644.93, 67109.65) * mm});
            skLineSegment(sketch, "E1156", {"start": v(47644.93, 67109.65) * mm, "end": v(47273.1, 67061) * mm});
            skLineSegment(sketch, "E1157", {"start": v(47273.1, 67061) * mm, "end": v(47169.33, 67854.25) * mm});
            skLineSegment(sketch, "E1158", {"start": v(36788.31, 55701.04) * mm, "end": v(36672.43, 56083.9) * mm});
            skLineSegment(sketch, "E1159", {"start": v(36672.43, 56083.9) * mm, "end": v(36816, 56127.34) * mm});
            skLineSegment(sketch, "E1160", {"start": v(36816, 56127.34) * mm, "end": v(36931.88, 55744.5) * mm});
            skLineSegment(sketch, "E1161", {"start": v(36931.88, 55744.5) * mm, "end": v(36788.31, 55701.04) * mm});
            skLineSegment(sketch, "E1162", {"start": v(54325.97, 61474.06) * mm, "end": v(54613.1, 61560.97) * mm});
            skLineSegment(sketch, "E1163", {"start": v(54613.1, 61560.97) * mm, "end": v(55047.66, 60125.3) * mm});
            skLineSegment(sketch, "E1164", {"start": v(55047.66, 60125.3) * mm, "end": v(54760.52, 60038.39) * mm});
            skLineSegment(sketch, "E1165", {"start": v(54760.52, 60038.39) * mm, "end": v(54325.97, 61474.06) * mm});
            skLineSegment(sketch, "E1166", {"start": v(41780.84, 66223.26) * mm, "end": v(42152.67, 66271.9) * mm});
            skLineSegment(sketch, "E1167", {"start": v(42152.67, 66271.9) * mm, "end": v(42256.44, 65478.66) * mm});
            skLineSegment(sketch, "E1168", {"start": v(42256.44, 65478.66) * mm, "end": v(41884.6, 65430.02) * mm});
            skLineSegment(sketch, "E1169", {"start": v(41884.6, 65430.02) * mm, "end": v(41780.84, 66223.26) * mm});
            skLineSegment(sketch, "E1170", {"start": v(37410.44, 55889.35) * mm, "end": v(37294.56, 56272.2) * mm});
            skLineSegment(sketch, "E1171", {"start": v(37294.56, 56272.2) * mm, "end": v(37438.13, 56315.65) * mm});
            skLineSegment(sketch, "E1172", {"start": v(37438.13, 56315.65) * mm, "end": v(37554, 55932.8) * mm});
            skLineSegment(sketch, "E1173", {"start": v(37554, 55932.8) * mm, "end": v(37410.44, 55889.35) * mm});
            skLineSegment(sketch, "E1174", {"start": v(38032.56, 56077.65) * mm, "end": v(37916.69, 56460.5) * mm});
            skLineSegment(sketch, "E1175", {"start": v(37916.69, 56460.5) * mm, "end": v(38155.97, 56532.92) * mm});
            skLineSegment(sketch, "E1176", {"start": v(38155.97, 56532.92) * mm, "end": v(38271.84, 56150.08) * mm});
            skLineSegment(sketch, "E1177", {"start": v(38271.84, 56150.08) * mm, "end": v(38032.56, 56077.65) * mm});
            skLineSegment(sketch, "E1178", {"start": v(55193.71, 59500.7) * mm, "end": v(54997.92, 59441.17) * mm});
            skLineSegment(sketch, "E1179", {"start": v(54997.92, 59441.17) * mm, "end": v(55097.59, 59262.42) * mm});
            skLineSegment(sketch, "E1180", {"start": v(55097.59, 59262.42) * mm, "end": v(55293.4, 59321.92) * mm});
            skLineSegment(sketch, "E1181", {"start": v(55293.4, 59321.92) * mm, "end": v(55193.71, 59500.7) * mm});
            skLineSegment(sketch, "E1182", {"start": v(44135.93, 60369.65) * mm, "end": v(43824.76, 60275.46) * mm});
            skLineSegment(sketch, "E1183", {"start": v(43824.76, 60275.46) * mm, "end": v(43535.06, 61232.58) * mm});
            skLineSegment(sketch, "E1184", {"start": v(43535.06, 61232.58) * mm, "end": v(43846.24, 61326.77) * mm});
            skLineSegment(sketch, "E1185", {"start": v(43846.24, 61326.77) * mm, "end": v(44135.93, 60369.65) * mm});
            skLineSegment(sketch, "E1186", {"start": v(45093.66, 60398.32) * mm, "end": v(44997.95, 60369.35) * mm});
            skLineSegment(sketch, "E1187", {"start": v(44997.95, 60369.35) * mm, "end": v(44925.53, 60608.63) * mm});
            skLineSegment(sketch, "E1188", {"start": v(44925.53, 60608.63) * mm, "end": v(45021.24, 60637.6) * mm});
            skLineSegment(sketch, "E1189", {"start": v(45021.24, 60637.6) * mm, "end": v(45093.66, 60398.32) * mm});
            skLineSegment(sketch, "E1190", {"start": v(57126.86, 66909.28) * mm, "end": v(57344.99, 67030.55) * mm});
            skLineSegment(sketch, "E1191", {"start": v(57344.99, 67030.55) * mm, "end": v(57466.47, 66812.05) * mm});
            skLineSegment(sketch, "E1192", {"start": v(57466.47, 66812.05) * mm, "end": v(57248.34, 66690.78) * mm});
            skLineSegment(sketch, "E1193", {"start": v(57248.34, 66690.78) * mm, "end": v(57126.86, 66909.28) * mm});
            skCircle(sketch, "E1194", {"center": v(57296.6, 66860.52) * mm, "radius": 100 * mm});
            skLineSegment(sketch, "E1195", {"start": v(48665.41, 64407.4) * mm, "end": v(50817.84, 65059.03) * mm});
            skLineSegment(sketch, "E1196", {"start": v(53236.72, 65072.83) * mm, "end": v(53523.86, 65159.74) * mm});
            skLineSegment(sketch, "E1197", {"start": v(53523.86, 65159.74) * mm, "end": v(54045.32, 63436.93) * mm});
            skLineSegment(sketch, "E1198", {"start": v(54045.32, 63436.93) * mm, "end": v(53758.18, 63350.02) * mm});
            skLineSegment(sketch, "E1199", {"start": v(53758.18, 63350.02) * mm, "end": v(53236.72, 65072.83) * mm});
            skLineSegment(sketch, "E1200", {"start": v(49601.8, 74661.76) * mm, "end": v(49677.77, 74066.6) * mm});
            skLineSegment(sketch, "E1201", {"start": v(49677.77, 74066.6) * mm, "end": v(49380.19, 74028.6) * mm});
            skLineSegment(sketch, "E1202", {"start": v(49380.19, 74028.6) * mm, "end": v(49304.21, 74623.77) * mm});
            skLineSegment(sketch, "E1203", {"start": v(60781.96, 51101.97) * mm, "end": v(61218.16, 51345.19) * mm});
            skLineSegment(sketch, "E1204", {"start": v(61218.16, 51345.19) * mm, "end": v(61461.66, 50908.48) * mm});
            skLineSegment(sketch, "E1205", {"start": v(61461.66, 50908.48) * mm, "end": v(61025.46, 50665.27) * mm});
            skLineSegment(sketch, "E1206", {"start": v(61025.46, 50665.27) * mm, "end": v(60781.96, 51101.97) * mm});
            skLineSegment(sketch, "E1207", {"start": v(56062.05, 59566.86) * mm, "end": v(56498.6, 59810.28) * mm});
            skLineSegment(sketch, "E1208", {"start": v(56498.6, 59810.28) * mm, "end": v(56742.1, 59373.58) * mm});
            skLineSegment(sketch, "E1209", {"start": v(56742.1, 59373.58) * mm, "end": v(56305.55, 59130.16) * mm});
            skLineSegment(sketch, "E1210", {"start": v(56305.55, 59130.16) * mm, "end": v(56062.05, 59566.86) * mm});
            skLineSegment(sketch, "E1211", {"start": v(58407.56, 55360.33) * mm, "end": v(58843.96, 55603.67) * mm});
            skLineSegment(sketch, "E1212", {"start": v(58843.96, 55603.67) * mm, "end": v(59087.46, 55166.97) * mm});
            skLineSegment(sketch, "E1213", {"start": v(59087.46, 55166.97) * mm, "end": v(58651.05, 54923.63) * mm});
            skLineSegment(sketch, "E1214", {"start": v(58651.05, 54923.63) * mm, "end": v(58407.56, 55360.33) * mm});
            skLineSegment(sketch, "E1215", {"start": v(50439.88, 69649.92) * mm, "end": v(50876.96, 69893.63) * mm});
            skLineSegment(sketch, "E1216", {"start": v(50876.96, 69893.63) * mm, "end": v(51120.46, 69456.93) * mm});
            skLineSegment(sketch, "E1217", {"start": v(51120.46, 69456.93) * mm, "end": v(50683.38, 69213.22) * mm});
            skLineSegment(sketch, "E1218", {"start": v(50683.38, 69213.22) * mm, "end": v(50439.88, 69649.92) * mm});
            skLineSegment(sketch, "E1219", {"start": v(53158.61, 64774.03) * mm, "end": v(53595.41, 65017.58) * mm});
            skLineSegment(sketch, "E1220", {"start": v(53595.41, 65017.58) * mm, "end": v(53838.91, 64580.88) * mm});
            skLineSegment(sketch, "E1221", {"start": v(53838.91, 64580.88) * mm, "end": v(53402.11, 64337.32) * mm});
            skLineSegment(sketch, "E1222", {"start": v(53402.11, 64337.32) * mm, "end": v(53158.61, 64774.03) * mm});
            skLineSegment(sketch, "E1223", {"start": v(49697.18, 72335.11) * mm, "end": v(49895.57, 72360.44) * mm});
            skLineSegment(sketch, "E1224", {"start": v(49895.57, 72360.44) * mm, "end": v(50013.33, 71437.92) * mm});
            skLineSegment(sketch, "E1225", {"start": v(50013.33, 71437.92) * mm, "end": v(49814.94, 71412.6) * mm});
            skLineSegment(sketch, "E1226", {"start": v(49814.94, 71412.6) * mm, "end": v(49697.18, 72335.11) * mm});
            skLineSegment(sketch, "E1227", {"start": v(53342.38, 67484.3) * mm, "end": v(54490.94, 68124.63) * mm});
            skLineSegment(sketch, "E1228", {"start": v(54490.94, 68124.63) * mm, "end": v(55131.28, 66976.06) * mm});
            skLineSegment(sketch, "E1229", {"start": v(55131.28, 66976.06) * mm, "end": v(53982.71, 66335.73) * mm});
            skLineSegment(sketch, "E1230", {"start": v(53982.71, 66335.73) * mm, "end": v(53342.38, 67484.3) * mm});
            skLineSegment(sketch, "E1231", {"start": v(59429.22, 56566.4) * mm, "end": v(60577.78, 57206.73) * mm});
            skLineSegment(sketch, "E1232", {"start": v(60577.78, 57206.73) * mm, "end": v(61218.11, 56058.17) * mm});
            skLineSegment(sketch, "E1233", {"start": v(61218.11, 56058.17) * mm, "end": v(60069.55, 55417.83) * mm});
            skLineSegment(sketch, "E1234", {"start": v(60069.55, 55417.83) * mm, "end": v(59429.22, 56566.4) * mm});
            skEllipse(sketch, "E1235", {"center": v(50534.92, 62319.96) * mm, "majorRadius": 158.75 * mm, "minorRadius": 158.75 * mm, "majorAxis": v(1, 0)});
            skArc(sketch, "E1236", {"start": v(50382.98, 62273.97) * mm, "mid": v(50460, 62180) * mm, "end": v(50580.9, 62168.02) * mm});
            skArc(sketch, "E1237", {"start": v(50686.86, 62365.95) * mm, "mid": v(50609.84, 62459.92) * mm, "end": v(50488.93, 62471.9) * mm});
            skLineSegment(sketch, "E1238", {"start": v(50580.9, 62168.02) * mm, "end": v(50488.93, 62471.9) * mm});
            skLineSegment(sketch, "E1239", {"start": v(50686.86, 62365.95) * mm, "end": v(50382.98, 62273.97) * mm});
            skLineSegment(sketch, "E1240", {"start": v(50488.93, 62471.9) * mm, "end": v(50146.36, 63603.7) * mm});
            skEllipse(sketch, "E1241", {"center": v(54694.5, 55886.04) * mm, "majorRadius": 158.75 * mm, "minorRadius": 158.75 * mm, "majorAxis": v(1, 0)});
            skArc(sketch, "E1242", {"start": v(54542.55, 55840.05) * mm, "mid": v(54619.57, 55746.08) * mm, "end": v(54740.48, 55734.1) * mm});
            skArc(sketch, "E1243", {"start": v(54846.43, 55932.03) * mm, "mid": v(54769.41, 56026) * mm, "end": v(54648.5, 56037.99) * mm});
            skLineSegment(sketch, "E1244", {"start": v(54740.48, 55734.1) * mm, "end": v(54648.5, 56037.99) * mm});
            skLineSegment(sketch, "E1245", {"start": v(54846.43, 55932.03) * mm, "end": v(54542.55, 55840.05) * mm});
            skLineSegment(sketch, "E1246", {"start": v(54648.5, 56037.99) * mm, "end": v(54305.93, 57169.78) * mm});
            skLineSegment(sketch, "E1247", {"start": v(53514.49, 50619.77) * mm, "end": v(53572.43, 50428.35) * mm});
            skLineSegment(sketch, "E1248", {"start": v(53572.43, 50428.35) * mm, "end": v(53457.57, 50393.59) * mm});
            skLineSegment(sketch, "E1249", {"start": v(53457.57, 50393.59) * mm, "end": v(53399.63, 50585.01) * mm});
            skLineSegment(sketch, "E1250", {"start": v(53399.63, 50585.01) * mm, "end": v(53514.49, 50619.77) * mm});
            skLineSegment(sketch, "E1251", {"start": v(53696.34, 50674.82) * mm, "end": v(53754.28, 50483.4) * mm});
            skLineSegment(sketch, "E1252", {"start": v(53754.28, 50483.4) * mm, "end": v(53639.42, 50448.63) * mm});
            skLineSegment(sketch, "E1253", {"start": v(53639.42, 50448.63) * mm, "end": v(53581.48, 50640.05) * mm});
            skLineSegment(sketch, "E1254", {"start": v(53581.48, 50640.05) * mm, "end": v(53696.34, 50674.82) * mm});
            skLineSegment(sketch, "E1255", {"start": v(53878.19, 50729.86) * mm, "end": v(53936.13, 50538.44) * mm});
            skLineSegment(sketch, "E1256", {"start": v(53936.13, 50538.44) * mm, "end": v(53821.28, 50503.67) * mm});
            skLineSegment(sketch, "E1257", {"start": v(53821.28, 50503.67) * mm, "end": v(53763.34, 50695.1) * mm});
            skLineSegment(sketch, "E1258", {"start": v(53763.34, 50695.1) * mm, "end": v(53878.19, 50729.86) * mm});
            skLineSegment(sketch, "E1259", {"start": v(68800.03, 49613.6) * mm, "end": v(52895.98, 44799.76) * mm});
            skLineSegment(sketch, "E1260", {"start": v(64824.99, 62739.91) * mm, "end": v(48922.75, 57926.63) * mm});
            skLineSegment(sketch, "E1261", {"start": v(63051.1, 64454.54) * mm, "end": v(48298.44, 59989.21) * mm});
            skLineSegment(sketch, "E1262", {"start": v(58279.05, 77095.62) * mm, "end": v(29227.41, 73368.86) * mm});
            skLineSegment(sketch, "E1263", {"start": v(50700.72, 66312.66) * mm, "end": v(57291.8, 44536.93) * mm});
            skLineSegment(sketch, "E1264", {"start": v(56137.88, 61183.94) * mm, "end": v(34457.3, 54621.67) * mm});
            skLineSegment(sketch, "E1265", {"start": v(53763.43, 65950.46) * mm, "end": v(32900.17, 59635.57) * mm});
            skLineSegment(sketch, "E1266", {"start": v(37800.23, 67883.79) * mm, "end": v(31024.37, 65832.87) * mm});
            skLineSegment(sketch, "E1267", {"start": v(61637.16, 69125.21) * mm, "end": v(32680.7, 60360.68) * mm});
            skLineSegment(sketch, "E1268", {"start": v(59917.1, 70856.14) * mm, "end": v(32056.39, 62423.27) * mm});
            skLineSegment(sketch, "E1269", {"start": v(58503.37, 75526.87) * mm, "end": v(30642.65, 67094) * mm});
            skLineSegment(sketch, "E1270", {"start": v(66863.03, 56006.6) * mm, "end": v(50960.79, 51193.3) * mm});
            skLineSegment(sketch, "E1271", {"start": v(67188.94, 54929.83) * mm, "end": v(51286.7, 50116.55) * mm});
            skLineSegment(sketch, "E1272", {"start": v(48161.86, 80551.5) * mm, "end": v(59147.71, 44256.2) * mm});
            skLineSegment(sketch, "E1273", {"start": v(46080.13, 79921.4) * mm, "end": v(50825.96, 64242) * mm});
            skLineSegment(sketch, "E1274", {"start": v(38710.33, 77690.7) * mm, "end": v(45197.28, 56258.97) * mm});
            skLineSegment(sketch, "E1275", {"start": v(32335.92, 75761.3) * mm, "end": v(38822.87, 54329.57) * mm});
            skLineSegment(sketch, "E1276", {"start": v(29943.13, 75037.05) * mm, "end": v(36430.08, 53605.32) * mm});
            skLineSegment(sketch, "E1277", {"start": v(67769.85, 47708.43) * mm, "end": v(50010.94, 79562.53) * mm});
            skCircle(sketch, "E1278", {"center": v(29827.25, 75419.9) * mm, "radius": 400 * mm});
            skCircle(sketch, "E1279", {"center": v(32220.04, 76144.15) * mm, "radius": 400 * mm});
            skCircle(sketch, "E1280", {"center": v(38594.44, 78073.55) * mm, "radius": 400 * mm});
            skCircle(sketch, "E1281", {"center": v(45967.29, 80305.16) * mm, "radius": 400 * mm});
            skCircle(sketch, "E1282", {"center": v(48042.95, 80933.4) * mm, "radius": 400 * mm});
            skCircle(sketch, "E1283", {"center": v(58675.8, 77146.49) * mm, "radius": 400 * mm});
            skCircle(sketch, "E1284", {"center": v(51669.85, 81022.14) * mm, "radius": 400 * mm});
            skCircle(sketch, "E1285", {"center": v(55953.69, 77875.9) * mm, "radius": 400 * mm});
            skCircle(sketch, "E1286", {"center": v(58886.21, 75642.75) * mm, "radius": 400 * mm});
            skCircle(sketch, "E1287", {"center": v(60299.95, 70972.02) * mm, "radius": 400 * mm});
            skCircle(sketch, "E1288", {"center": v(62020, 69241.1) * mm, "radius": 400 * mm});
            skCircle(sketch, "E1289", {"center": v(63433.94, 64570.42) * mm, "radius": 400 * mm});
            skCircle(sketch, "E1290", {"center": v(65207.84, 62855.8) * mm, "radius": 400 * mm});
            skCircle(sketch, "E1291", {"center": v(66621.57, 58185.06) * mm, "radius": 400 * mm});
            skCircle(sketch, "E1292", {"center": v(67245.88, 56122.47) * mm, "radius": 400 * mm});
            skCircle(sketch, "E1293", {"center": v(69182.88, 49729.47) * mm, "radius": 400 * mm});
            skCircle(sketch, "E1294", {"center": v(28686.24, 72177.64) * mm, "radius": 400 * mm});
            skCircle(sketch, "E1295", {"center": v(30641.28, 65716.92) * mm, "radius": 400 * mm});
            skCircle(sketch, "E1296", {"center": v(32515.18, 59519.04) * mm, "radius": 400 * mm});
            skCircle(sketch, "E1297", {"center": v(34071.81, 54504.99) * mm, "radius": 400 * mm});
            skCircle(sketch, "E1298", {"center": v(48987.18, 56326.68) * mm, "radius": 400 * mm});
            skCircle(sketch, "E1299", {"center": v(49399.16, 79054.72) * mm, "radius": 400 * mm});
            skLineSegment(sketch, "E1300", {"start": v(36305.06, 74483.7) * mm, "end": v(29069.58, 72293.67) * mm});
            skLineSegment(sketch, "E1301", {"start": v(66238.73, 58069.18) * mm, "end": v(50336.48, 53255.9) * mm});
            skLineSegment(sketch, "E1302", {"start": v(53375.44, 75865.5) * mm, "end": v(51312.22, 74715.25) * mm});
            skLineSegment(sketch, "E1303", {"start": v(51499.4, 78348.17) * mm, "end": v(51983.24, 74576.36) * mm});
            skLineSegment(sketch, "E1304", {"start": v(35636.54, 59235.4) * mm, "end": v(51432.72, 80700.01) * mm});
            skLineSegment(sketch, "E1305", {"start": v(39916.94, 56084.63) * mm, "end": v(55716.5, 77553.82) * mm});
            skCircle(sketch, "E1306", {"center": v(67571.79, 55045.71) * mm, "radius": 400 * mm});
            skCircle(sketch, "E1307", {"center": v(65653.83, 61371.34) * mm, "radius": 400 * mm});
            skCircle(sketch, "E1308", {"center": v(63682.27, 63752.25) * mm, "radius": 400 * mm});
            skLineSegment(sketch, "E1309", {"start": v(65270.99, 61255.46) * mm, "end": v(49371.78, 56443.1) * mm});
            skCircle(sketch, "E1310", {"center": v(57407.68, 44154.09) * mm, "radius": 400 * mm});
            skCircle(sketch, "E1311", {"center": v(54584.18, 43299.47) * mm, "radius": 400 * mm});
            skCircle(sketch, "E1312", {"center": v(67964.63, 47359.05) * mm, "radius": 400 * mm});
            skLineSegment(sketch, "E1313", {"start": v(54468.58, 43682.4) * mm, "end": v(49533.34, 59987.56) * mm});
            skLineSegment(sketch, "E1314", {"start": v(67004.16, 47476.67) * mm, "end": v(49593.94, 78705.35) * mm});
            skCircle(sketch, "E1315", {"center": v(49816.16, 79911.9) * mm, "radius": 400 * mm});
            skCircle(sketch, "E1316", {"center": v(67198.94, 47127.3) * mm, "radius": 400 * mm});
            skLineSegment(sketch, "E1317", {"start": v(63299.42, 63636.4) * mm, "end": v(48546.14, 59170.88) * mm});
            skSolve(sketch);
        }
        {
            var Q0;
            Q0=qCreatedBy(makeId("Top.planeOp"),FACE);
            var sketch = newSketch(context, id + "F2", { "sketchPlane" : qUnion([Q0])});
            skLineSegment(sketch, "E1318.0", {"start": v(54145.32, 46326.6) * mm, "end": v(52902.06, 50434.12) * mm});
            skLineSegment(sketch, "E1318.1", {"start": v(67150.92, 50263.13) * mm, "end": v(54431.42, 46413.2) * mm});
            skLineSegment(sketch, "E1318.2", {"start": v(67150.92, 50263.13) * mm, "end": v(54145.32, 46326.6) * mm});
            skLineSegment(sketch, "E1318.3", {"start": v(53909.98, 50739.2) * mm, "end": v(57604, 51858.9) * mm});
            skLineSegment(sketch, "E1318.4", {"start": v(53075.2, 75510.7) * mm, "end": v(67150.92, 50263.13) * mm});
            skLineSegment(sketch, "E1318.5", {"start": v(54874.02, 59663.37) * mm, "end": v(58991.9, 52278.2) * mm});
            skLineSegment(sketch, "E1318.6", {"start": v(54760.52, 60038.39) * mm, "end": v(54325.97, 61474.06) * mm});
            skLineSegment(sketch, "E1318.7", {"start": v(53225.02, 65066.3) * mm, "end": v(53000.6, 65468.81) * mm});
            skLineSegment(sketch, "E1318.9", {"start": v(49304.21, 74623.77) * mm, "end": v(49909.66, 69880.9) * mm});
            skLineSegment(sketch, "E1318.10", {"start": v(49253.57, 75020.46) * mm, "end": v(53075.2, 75510.7) * mm});
            skLineSegment(sketch, "E1319", {"start": v(50281.68, 69933.64) * mm, "end": v(49909.66, 69880.9) * mm});
            skLineSegment(sketch, "E1320", {"start": v(54325.97, 61474.06) * mm, "end": v(53225.02, 65066.3) * mm});
            skLineSegment(sketch, "E1321", {"start": v(53000.6, 65468.81) * mm, "end": v(50281.68, 69933.64) * mm});
            skLineSegment(sketch, "E1322", {"start": v(54874.02, 59663.37) * mm, "end": v(54760.52, 60038.39) * mm});
            skLineSegment(sketch, "E1323", {"start": v(49304.21, 74623.77) * mm, "end": v(49253.57, 75020.46) * mm});
            skLineSegment(sketch, "E1324", {"start": v(53909.98, 50739.2) * mm, "end": v(52902.06, 50434.12) * mm});
            skLineSegment(sketch, "E1325", {"start": v(58991.9, 52278.2) * mm, "end": v(57604, 51858.9) * mm});
            skLineSegment(sketch, "E1326", {"start": v(53342.81, 50358.57) * mm, "end": v(59287.5, 52158.7) * mm});
            skLineSegment(sketch, "E1327", {"start": v(54412.26, 46825.31) * mm, "end": v(53342.81, 50358.57) * mm});
            skLineSegment(sketch, "E1328", {"start": v(54412.26, 46825.31) * mm, "end": v(66559.72, 50502.1) * mm});
            skLineSegment(sketch, "E1329", {"start": v(52857.63, 75079.51) * mm, "end": v(66559.72, 50502.1) * mm});
            skLineSegment(sketch, "E1330", {"start": v(49601.8, 74661.76) * mm, "end": v(52857.63, 75079.51) * mm});
            skLineSegment(sketch, "E1331", {"start": v(50131.26, 70514.15) * mm, "end": v(49601.8, 74661.76) * mm});
            skLineSegment(sketch, "E1332", {"start": v(50504.39, 70561.9) * mm, "end": v(50131.26, 70514.15) * mm});
            skLineSegment(sketch, "E1333", {"start": v(50504.39, 70561.9) * mm, "end": v(53523.86, 65159.74) * mm});
            skLineSegment(sketch, "E1334", {"start": v(55070.83, 59721.1) * mm, "end": v(53523.86, 65159.74) * mm});
            skLineSegment(sketch, "E1335", {"start": v(59287.5, 52158.7) * mm, "end": v(55070.83, 59721.1) * mm});
            skSolve(sketch);
        }
        {
            var Q0;
            Q0 = qSketchRegion(id + "F2", true);
            extrude(context, id + "F3", {"entities" : qUnion([Q0]), "depth" : (getVariable(context, 'Ceiling')) * mm, "offsetDistance" : 25 * mm});
        }
        {
            var Q0;
            Q0=qCreatedBy(makeId("Top.planeOp"),FACE);
            var sketch = newSketch(context, id + "F4", { "sketchPlane" : qUnion([Q0])});
            skLineSegment(sketch, "E1336.0", {"start": v(54874.02, 59663.37) * mm, "end": v(58991.9, 52278.2) * mm});
            skLineSegment(sketch, "E1336.1", {"start": v(58991.9, 52278.2) * mm, "end": v(57604, 51858.9) * mm});
            skLineSegment(sketch, "E1336.2", {"start": v(53909.98, 50739.2) * mm, "end": v(57604, 51858.9) * mm});
            skLineSegment(sketch, "E1336.3", {"start": v(53909.98, 50739.2) * mm, "end": v(52902.06, 50434.12) * mm});
            skLineSegment(sketch, "E1336.4", {"start": v(54145.32, 46326.6) * mm, "end": v(52902.06, 50434.12) * mm});
            skLineSegment(sketch, "E1336.5", {"start": v(67150.92, 50263.13) * mm, "end": v(54145.32, 46326.6) * mm});
            skLineSegment(sketch, "E1336.6", {"start": v(53075.2, 75510.7) * mm, "end": v(67150.92, 50263.13) * mm});
            skLineSegment(sketch, "E1337.0", {"start": v(54874.02, 59663.37) * mm, "end": v(54760.52, 60038.39) * mm});
            skLineSegment(sketch, "E1337.1", {"start": v(54760.52, 60038.39) * mm, "end": v(54325.97, 61474.06) * mm});
            skLineSegment(sketch, "E1337.2", {"start": v(54325.97, 61474.06) * mm, "end": v(53225.02, 65066.3) * mm});
            skLineSegment(sketch, "E1337.3", {"start": v(53000.6, 65468.81) * mm, "end": v(50281.68, 69933.64) * mm});
            skLineSegment(sketch, "E1337.4", {"start": v(53225.02, 65066.3) * mm, "end": v(53000.6, 65468.81) * mm});
            skLineSegment(sketch, "E1337.5", {"start": v(50281.68, 69933.64) * mm, "end": v(49909.66, 69880.9) * mm});
            skLineSegment(sketch, "E1337.6", {"start": v(49304.21, 74623.77) * mm, "end": v(49909.66, 69880.9) * mm});
            skLineSegment(sketch, "E1337.7", {"start": v(49304.21, 74623.77) * mm, "end": v(49253.57, 75020.46) * mm});
            skLineSegment(sketch, "E1337.8", {"start": v(49253.57, 75020.46) * mm, "end": v(53075.2, 75510.7) * mm});
            skSolve(sketch);
        }
        {
            var Q0;
            Q0 = qSketchRegion(id + "F4", true);
            extrude(context, id + "F5", {"entities" : qUnion([Q0]), "oppositeDirection" : true, "depth" : 25 * mm, "offsetDistance" : 25 * mm});
        }
        {
            var Q0;
            Q0=qCreatedBy(makeId("Top.planeOp"),FACE);
            var sketch = newSketch(context, id + "F6", { "sketchPlane" : qUnion([Q0])});
            skLineSegment(sketch, "E1338.0", {"start": v(62899.33, 55116.74) * mm, "end": v(63167.18, 54636.37) * mm});
            skLineSegment(sketch, "E1338.1", {"start": v(62948.82, 54514.62) * mm, "end": v(63167.18, 54636.37) * mm});
            skLineSegment(sketch, "E1338.2", {"start": v(62680.98, 54995) * mm, "end": v(62948.82, 54514.62) * mm});
            skLineSegment(sketch, "E1338.3", {"start": v(62680.98, 54995) * mm, "end": v(62899.33, 55116.74) * mm});
            skLineSegment(sketch, "E1338.4", {"start": v(61874.42, 56441.78) * mm, "end": v(62092.77, 56563.53) * mm});
            skLineSegment(sketch, "E1338.5", {"start": v(61606.57, 56922.15) * mm, "end": v(61824.92, 57043.9) * mm});
            skLineSegment(sketch, "E1338.6", {"start": v(61824.92, 57043.9) * mm, "end": v(62092.77, 56563.53) * mm});
            skLineSegment(sketch, "E1338.7", {"start": v(61606.57, 56922.15) * mm, "end": v(61874.42, 56441.78) * mm});
            skPoint(sketch, "E1338.8", {"position": v(61983.6, 56502.65) * mm});
            skLineSegment(sketch, "E1339.0", {"start": v(59826.06, 53123.27) * mm, "end": v(60131.76, 53293.71) * mm});
            skLineSegment(sketch, "E1339.1", {"start": v(60131.76, 53293.71) * mm, "end": v(60570.05, 52507.65) * mm});
            skLineSegment(sketch, "E1339.2", {"start": v(60264.36, 52337.2) * mm, "end": v(60570.05, 52507.65) * mm});
            skLineSegment(sketch, "E1339.3", {"start": v(59826.06, 53123.27) * mm, "end": v(60264.36, 52337.2) * mm});
            skLineSegment(sketch, "E1340.0", {"start": v(56060.35, 60596.37) * mm, "end": v(56498.65, 59810.3) * mm});
            skPoint(sketch, "E1340.1", {"position": v(56060.35, 60596.37) * mm});
            skLineSegment(sketch, "E1340.2", {"start": v(55754.66, 60425.92) * mm, "end": v(56060.35, 60596.37) * mm});
            skLineSegment(sketch, "E1340.3", {"start": v(55754.66, 60425.92) * mm, "end": v(56192.96, 59639.86) * mm});
            skLineSegment(sketch, "E1340.4", {"start": v(56192.96, 59639.86) * mm, "end": v(56498.65, 59810.3) * mm});
            skLineSegment(sketch, "E1340.5", {"start": v(59174.97, 61283.7) * mm, "end": v(59393.32, 61405.46) * mm});
            skLineSegment(sketch, "E1340.6", {"start": v(59442.82, 60803.34) * mm, "end": v(59661.17, 60925.09) * mm});
            skLineSegment(sketch, "E1340.7", {"start": v(59174.97, 61283.7) * mm, "end": v(59442.82, 60803.34) * mm});
            skLineSegment(sketch, "E1340.8", {"start": v(59393.32, 61405.46) * mm, "end": v(59661.17, 60925.09) * mm});
            skLineSegment(sketch, "E1340.9", {"start": v(58318.92, 63332.61) * mm, "end": v(58586.76, 62852.24) * mm});
            skLineSegment(sketch, "E1340.10", {"start": v(58100.57, 63210.86) * mm, "end": v(58318.92, 63332.61) * mm});
            skLineSegment(sketch, "E1340.11", {"start": v(58100.57, 63210.86) * mm, "end": v(58368.41, 62730.5) * mm});
            skLineSegment(sketch, "E1340.12", {"start": v(58368.41, 62730.5) * mm, "end": v(58586.76, 62852.24) * mm});
            skPoint(sketch, "E1340.13", {"position": v(56279.5, 60203.34) * mm});
            skPoint(sketch, "E1340.14", {"position": v(59527.24, 61165.27) * mm});
            skSolve(sketch);
        }
        {
            var Q0;
            Q0 = qSketchRegion(id + "F6", true);
            extrude(context, id + "F7", {"entities" : qUnion([Q0]), "operationType" : NewBodyOperationType.ADD, "depth" : (getVariable(context, 'Ceiling')) * mm, "offsetDistance" : 25 * mm});
        }
        {
            var Q0;
            Q0=qCreatedBy(makeId("Top.planeOp"),FACE);
            var sketch = newSketch(context, id + "F8", { "sketchPlane" : qUnion([Q0])});
            skLineSegment(sketch, "E1341.0", {"start": v(64867.16, 51074.04) * mm, "end": v(51575.28, 74914.98) * mm, "construction": true});
            skPoint(sketch, "E1342.0", {"position": v(56060.35, 60596.37) * mm});
            skLineSegment(sketch, "E1343", {"start": v(56060.35, 60596.37) * mm, "end": v(58728.8, 62084.09) * mm});
            skLineSegment(sketch, "E1344.0", {"start": v(61899.36, 49097.97) * mm, "end": v(50281.68, 69933.64) * mm, "construction": true});
            skLineSegment(sketch, "E1345", {"start": v(58565.38, 55077.28) * mm, "end": v(61670.18, 56808.28) * mm});
            skLineSegment(sketch, "E1346", {"start": v(61670.18, 56808.28) * mm, "end": v(58728.8, 62084.09) * mm});
            skLineSegment(sketch, "E1347.0", {"start": v(55070.83, 59721.1) * mm, "end": v(53523.86, 65159.74) * mm, "construction": true});
            skLineSegment(sketch, "E1347.1", {"start": v(55070.83, 59721.1) * mm, "end": v(59287.5, 52158.7) * mm, "construction": true});
            skLineSegment(sketch, "E1348", {"start": v(55754.66, 60425.92) * mm, "end": v(54991.4, 60000.34) * mm});
            skLineSegment(sketch, "E1349", {"start": v(54991.4, 60000.34) * mm, "end": v(55070.83, 59721.1) * mm});
            skLineSegment(sketch, "E1350", {"start": v(58565.38, 55077.28) * mm, "end": v(57874.84, 54692.24) * mm});
            skLineSegment(sketch, "E1351", {"start": v(57874.84, 54692.24) * mm, "end": v(55102.82, 59663.72) * mm});
            skLineSegment(sketch, "E1352", {"start": v(55102.82, 59663.72) * mm, "end": v(55070.83, 59721.1) * mm});
            skLineSegment(sketch, "E1353.0", {"start": v(55754.66, 60425.92) * mm, "end": v(56192.96, 59639.86) * mm});
            skLineSegment(sketch, "E1353.1", {"start": v(56192.96, 59639.86) * mm, "end": v(56498.65, 59810.3) * mm});
            skLineSegment(sketch, "E1353.2", {"start": v(56060.35, 60596.37) * mm, "end": v(56498.65, 59810.3) * mm});
            skSolve(sketch);
        }
        {
            var Q0;
            Q0 = qSketchRegion(id + "F8", true);
            extrude(context, id + "F9", {"entities" : qUnion([Q0]), "depth" : 150 * mm, "offsetDistance" : 25 * mm});
        }
        {
            var Q0;
            Q0=makeQuery(id+"F5.opExtrude","CAP_FACE",FACE,{"disambiguationData":[OSD([sQuery(id+"F4.wireOp",EDGE,"E1336.0"),sQuery(id+"F4.wireOp",EDGE,"E1336.1"),sQuery(id+"F4.wireOp",EDGE,"E1336.2"),sQuery(id+"F4.wireOp",EDGE,"E1336.3"),sQuery(id+"F4.wireOp",EDGE,"E1336.4"),sQuery(id+"F4.wireOp",EDGE,"E1336.5"),sQuery(id+"F4.wireOp",EDGE,"E1336.6"),sQuery(id+"F4.wireOp",EDGE,"E1337.0"),sQuery(id+"F4.wireOp",EDGE,"E1337.1"),sQuery(id+"F4.wireOp",EDGE,"E1337.2"),sQuery(id+"F4.wireOp",EDGE,"E1337.3"),sQuery(id+"F4.wireOp",EDGE,"E1337.4"),sQuery(id+"F4.wireOp",EDGE,"E1337.5"),sQuery(id+"F4.wireOp",EDGE,"E1337.6"),sQuery(id+"F4.wireOp",EDGE,"E1337.7"),sQuery(id+"F4.wireOp",EDGE,"E1337.8")])],"isStart":true});
            var sketch = newSketch(context, id + "F10", { "sketchPlane" : qUnion([Q0])});
            skLineSegment(sketch, "E1354.0", {"start": v(60028.23, 54193.42) * mm, "end": v(59168.74, 53933.32) * mm});
            skLineSegment(sketch, "E1354.1", {"start": v(59168.74, 53933.32) * mm, "end": v(58821.16, 55081.88) * mm});
            skLineSegment(sketch, "E1354.2", {"start": v(58821.16, 55081.88) * mm, "end": v(59680.65, 55341.98) * mm});
            skLineSegment(sketch, "E1354.3", {"start": v(59680.65, 55341.98) * mm, "end": v(60028.23, 54193.42) * mm});
            skSolve(sketch);
        }
        {
            var Q0;
            Q0 = qSketchRegion(id + "F10", true);
            extrude(context, id + "F11", {"entities" : qUnion([Q0]), "operationType" : NewBodyOperationType.REMOVE, "endBound" : BoundingType.THROUGH_ALL, "oppositeDirection" : true, "depth" : 25 * mm, "offsetDistance" : 25 * mm});
        }
    });
